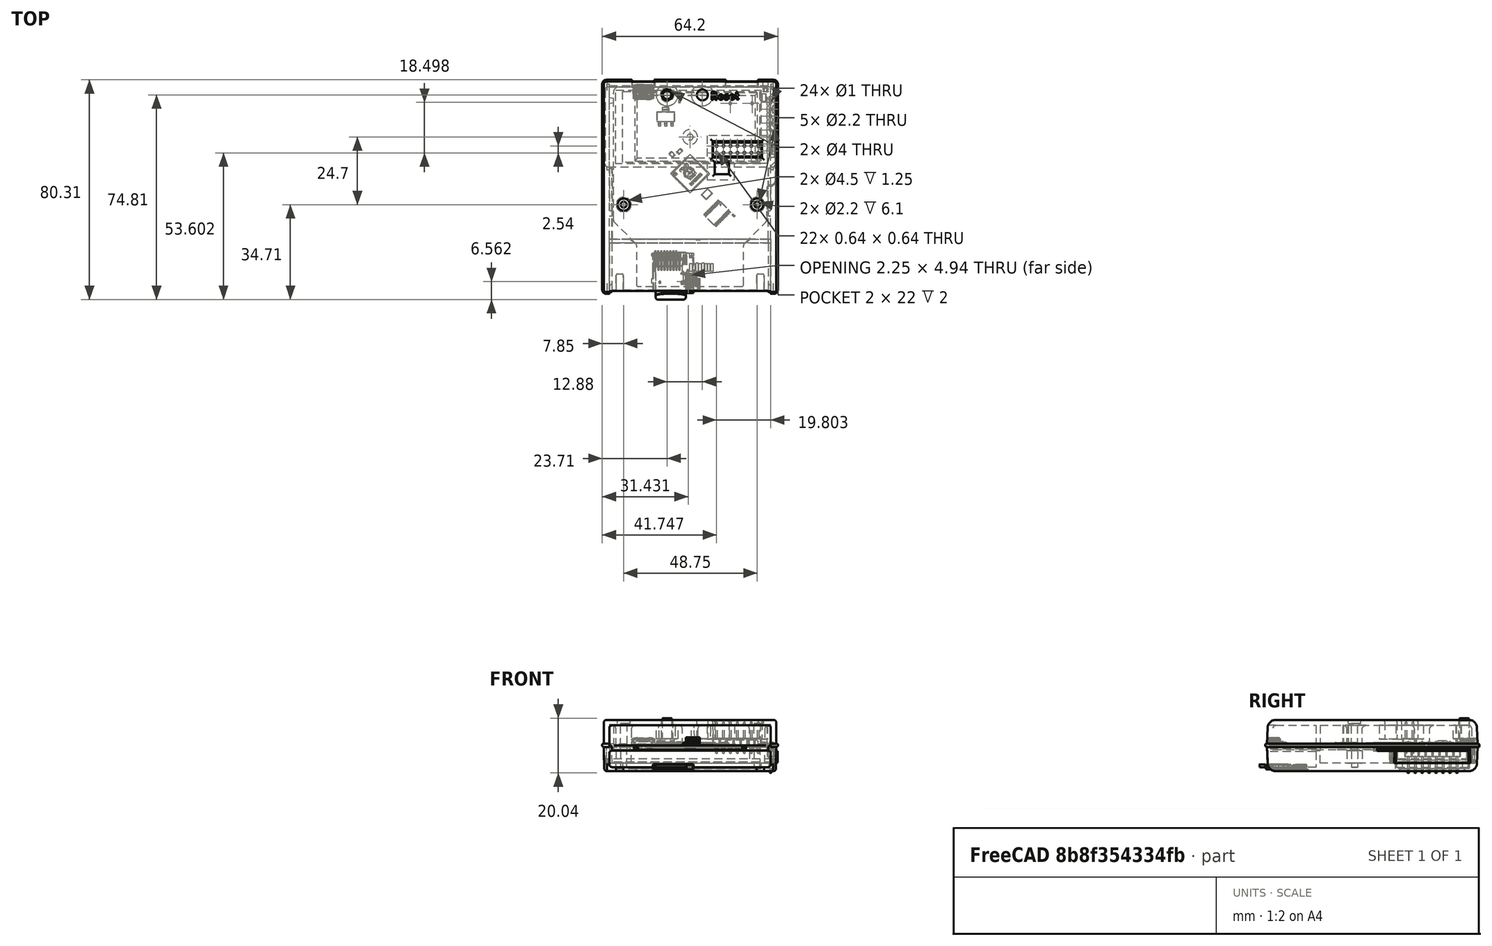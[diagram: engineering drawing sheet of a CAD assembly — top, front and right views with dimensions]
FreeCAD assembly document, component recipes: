
FREECAD ASSEMBLY — COMPONENT RECIPES ("DecentCart2350")

This assembly document has 7 components, labeled P0..P6 below (a component is one placed body or linked part). 7 of them carry a construction recipe — the FreeCAD feature program that regenerates the part from scratch, quoted from this document or its linked companion documents; the rest are supplied as boundary geometry only. No exploded tour is included for this assembly.
COMPONENT P0 — recipe-attached ("DecentCart", modeled in this document).
Construction recipe (the document's own serialized feature program — sketch geometry with constraints, then the solid features built on it; lengths are millimeters unless a unit is written):

FEATURE [PartDesign::SubShapeBinder] Binder009
  BindCopyOnChange = 0
  BindMode = 0
  ClaimChildren = false
  Context = -> Board_9dbe [Body004.Binder009.]
  Fuse = false
  MakeFace = true
  OffsetFill = false
  OffsetIntersection = false
  OffsetJoinType = 0
  OffsetOpenResult = false
  PartialLoad = false
  Relative = true
  Support = -> [Board_Geoms_9dbe[PCB_Sketch_9dbe.]]
  _Version = 2
FEATURE [Sketcher::SketchObject] Sketch028
  ArcFitTolerance = 1e-06
  AttachmentOffset = pos=(0,0,-4.95) rot=(0,0,1;0rad)
  AttachmentSupport = -> [XY_Plane]
  ExternalGeometry = -> [Binder009]
  FullyConstrained = true
  MakeInternals = false
  MapMode = 5
  Placement = pos=(0,0,-4.95) rot=(0,0,1;0rad)
  sketch-geometry (10):
    g0: LineSegment StartX=30.25 StartY=70 StartZ=0 EndX=-30.05 EndY=70 EndZ=0
    g1: LineSegment StartX=-31.05 StartY=69 StartZ=0 EndX=-31.05 EndY=41.8 EndZ=0
    g2: LineSegment StartX=-30.05 StartY=40.8 StartZ=0 EndX=30.25 EndY=40.8 EndZ=0
    g3: LineSegment StartX=31.25 StartY=41.8 StartZ=0 EndX=31.25 EndY=69 EndZ=0
    g4: ArcOfCircle CenterX=30.25 CenterY=69 CenterZ=0 NormalX=0 NormalY=0 NormalZ=1 AngleXU=0 Radius=1 StartAngle=1.6e-15 EndAngle=1.5708
    g5: ArcOfCircle CenterX=-30.05 CenterY=69 CenterZ=0 NormalX=0 NormalY=0 NormalZ=1 AngleXU=0 Radius=1 StartAngle=1.5708 EndAngle=3.14159
    g6: ArcOfCircle CenterX=-30.05 CenterY=41.8 CenterZ=0 NormalX=0 NormalY=0 NormalZ=1 AngleXU=0 Radius=1 StartAngle=3.14159 EndAngle=4.71239
    g7: ArcOfCircle CenterX=30.25 CenterY=41.8 CenterZ=0 NormalX=0 NormalY=0 NormalZ=1 AngleXU=0 Radius=1 StartAngle=4.71239 EndAngle=6.28319
    g8: GeomPoint [constr] X=31.25 Y=70 Z=0
    g9: GeomPoint [constr] X=-31.05 Y=40.8 Z=0
  constraints (24):
    c: Tangent(g0,g4) = -1.5708
    c: Tangent(g0,g5) = -1.5708
    c: Tangent(g1,g5) = -1.5708
    c: Tangent(g1,g6) = -1.5708
    c: Tangent(g2,g6) = -1.5708
    c: Tangent(g2,g7) = -1.5708
    c: Tangent(g3,g7) = -1.5708
    c: Tangent(g3,g4) = -1.5708
    c: Horizontal(g0)
    c: Horizontal(g2)
    c: Vertical(g1)
    c: Vertical(g3)
    c: Equal(g4,g5)
    c: Equal(g5,g6)
    c: Equal(g6,g7)
    c: PointOnObject(g8,g0)
    c: PointOnObject(g8,g3)
    c: PointOnObject(g9,g1)
    c: PointOnObject(g9,g2)
    c: Radius(g5) = 1
    c: PointOnObject(g3,g-3)
    c: PointOnObject(g0,g-4)
    c: DistanceX(g1,g3) = 62.3
    c: DistanceY(g2,g0) = 29.2
FEATURE [PartDesign::Pad] Pad018  label="Display PCB"
  Direction = (0,0,1)
  Length = 1.25
  Length2 = 10
  Profile = -> Sketch028
  ReferenceAxis = -> Sketch028 [N_Axis]
  Reversed = true
  Suppressed = false
  Type = 0
FEATURE [Sketcher::SketchObject] Sketch029
  ArcFitTolerance = 1e-06
  AttachmentSupport = -> [Pad018]
  ExternalGeometry = -> [Pad018]
  FullyConstrained = true
  MakeInternals = false
  MapMode = 5
  Placement = pos=(0,0,-6.2) rot=(1,0,0;3.14159rad)
  sketch-geometry (8):
    g0: LineSegment StartX=-24.65 StartY=-42.4 StartZ=0 EndX=-24.65 EndY=-68.4 EndZ=0
    g1: LineSegment StartX=-24.65 StartY=-68.4 StartZ=0 EndX=25.35 EndY=-68.4 EndZ=0
    g2: LineSegment StartX=25.35 StartY=-68.4 StartZ=0 EndX=25.35 EndY=-42.4 EndZ=0
    g3: LineSegment StartX=25.35 StartY=-42.4 StartZ=0 EndX=-24.65 EndY=-42.4 EndZ=0
    g4: GeomPoint [constr] X=0.1 Y=-55.4 Z=0
    g5: GeomPoint [constr] X=-31.05 Y=-55.4 Z=0
    g6: GeomPoint [constr] X=31.25 Y=-55.4 Z=0
    g7: LineSegment [constr] StartX=-31.05 StartY=-55.4 StartZ=0 EndX=31.25 EndY=-55.4 EndZ=0
  constraints (16):
    c: Coincident(g0,g1)
    c: Coincident(g1,g2)
    c: Coincident(g2,g3)
    c: Coincident(g3,g0)
    c: Vertical(g2)
    c: Horizontal(g1)
    c: Horizontal(g3)
    c: DistanceX(g3,g3) = 50
    c: DistanceY(g2,g2) = 26
    c: Symmetric(g-3,g-4,g4)
    c: Symmetric(g-3,g-3,g5)
    c: Symmetric(g-4,g-4,g6)
    c: Coincident(g7,g5)
    c: Coincident(g7,g6)
    c: Symmetric(g0,g0,g7)
    c: DistanceX(g-3,g0) = 6.4
FEATURE [PartDesign::Pad] Pad019  label="Display glass"
  BaseFeature = -> Pad018
  Direction = (0,0,-1)
  Length = 2
  Length2 = 10
  Profile = -> Sketch029
  ReferenceAxis = -> Sketch029 [N_Axis]
  Suppressed = false
  Type = 0
FEATURE [Sketcher::SketchObject] Sketch030  label="Display area"
  ArcFitTolerance = 1e-06
  AttachmentSupport = -> [Pad019]
  ExternalGeometry = -> [Pad019]
  FullyConstrained = true
  MakeInternals = false
  MapMode = 5
  Placement = pos=(0,0,-8.2) rot=(1,0,0;3.14159rad)
  sketch-geometry (7):
    g0: LineSegment StartX=-19.3 StartY=-43.9 StartZ=0 EndX=-19.3 EndY=-66.9 EndZ=0
    g1: LineSegment StartX=-19.3 StartY=-66.9 StartZ=0 EndX=23.7 EndY=-66.9 EndZ=0
    g2: LineSegment StartX=23.7 StartY=-66.9 StartZ=0 EndX=23.7 EndY=-43.9 EndZ=0
    g3: LineSegment StartX=23.7 StartY=-43.9 StartZ=0 EndX=-19.3 EndY=-43.9 EndZ=0
    g4: GeomPoint [constr] X=-31.05 Y=-55.4 Z=0
    g5: GeomPoint [constr] X=31.25 Y=-55.4 Z=0
    g6: LineSegment [constr] StartX=-31.05 StartY=-55.4 StartZ=0 EndX=31.25 EndY=-55.4 EndZ=0
  constraints (15):
    c: Coincident(g0,g1)
    c: Coincident(g1,g2)
    c: Coincident(g2,g3)
    c: Coincident(g3,g0)
    c: Vertical(g2)
    c: Horizontal(g1)
    c: Horizontal(g3)
    c: DistanceX(g3,g3) = 43
    c: DistanceY(g2,g2) = 23
    c: Symmetric(g-3,g-3,g4)
    c: Symmetric(g-4,g-4,g5)
    c: Coincident(g6,g4)
    c: Coincident(g6,g5)
    c: Symmetric(g0,g0,g6)
    c: DistanceX(g-3,g0) = 11.75
FEATURE [PartDesign::Body] Body004  label="Display"
  AllowCompound = false
  Group = -> [Binder009,Sketch028,Pad018,Sketch029,Pad019,Sketch030]
  Origin = -> Origin
  Tip = -> Pad019
COMPONENT P1 — recipe-attached ("BackBody", modeled in this document).
Construction recipe (the document's own serialized feature program — sketch geometry with constraints, then the solid features built on it; lengths are millimeters unless a unit is written):

FEATURE [Sketcher::SketchObject] Sketch
  ArcFitTolerance = 1e-06
  AttachmentSupport = -> [YZ_Plane008]
  FullyConstrained = true
  MakeInternals = false
  MapMode = 5
  Placement = pos=(0,0,0) rot=(0.57735,0.57735,0.57735;2.0944rad)
  sketch-geometry (7):
    g0: LineSegment StartX=-5 StartY=0 StartZ=0 EndX=-4.75 EndY=6.36769 EndZ=0
    g1: ArcOfCircle CenterX=-1.75231 CenterY=6.25 CenterZ=0 NormalX=0 NormalY=0 NormalZ=1 AngleXU=0 Radius=3 StartAngle=1.5708 EndAngle=3.10235
    g2: LineSegment StartX=-1.75231 StartY=9.25 StartZ=0 EndX=68.7523 EndY=9.25 EndZ=0
    g3: ArcOfCircle CenterX=68.7523 CenterY=6.25 CenterZ=0 NormalX=0 NormalY=0 NormalZ=1 AngleXU=0 Radius=3 StartAngle=0.0392405 EndAngle=1.5708
    g4: LineSegment StartX=71.75 StartY=6.36769 StartZ=0 EndX=72 EndY=0 EndZ=0
    g5: LineSegment StartX=72 StartY=0 StartZ=0 EndX=-5 EndY=0 EndZ=0
    g6: LineSegment [constr] StartX=33.5 StartY=0 StartZ=0 EndX=33.5 EndY=9.25 EndZ=0
  constraints (18):
    c: PointOnObject(g0,g-1)
    c: Tangent(g0,g1) = 1.5708
    c: Horizontal(g2)
    c: Tangent(g2,g3) = 1.5708
    c: Coincident(g4,g5)
    c: Coincident(g5,g0)
    c: Tangent(g3,g4) = 1.5708
    c: Tangent(g1,g2) = 1.5708
    c: Horizontal(g0,g3)
    c: Radius(g1) = 3
    c: DistanceX(g0,g3) = 76.5
    c: DistanceX(g0,g4) = 77
    c: PointOnObject(g6,g2)
    c: Symmetric(g1,g2,g6)
    c: DistanceY(g4,g2) = 9.25
    c: DistanceX(g0,g-3) = 5
    c: Symmetric(g0,g4,g6)
    c: PointOnObject(g6,g-1)
FEATURE [PartDesign::Pad] Pad  label="General shape of the thing"
  Direction = (1,0,0)
  Length = 63
  Length2 = 10
  Midplane = true
  Placement = pos=(0,0,0) rot=(1,1,1;2.0944rad)
  Profile = -> Sketch
  ReferenceAxis = -> Sketch [N_Axis]
  Suppressed = false
  Type = 0
FEATURE [PartDesign::Point] DatumPoint  label="Top middle"
  AttacherType = Attacher::AttachEnginePoint
  MapMode = 37
  Placement = pos=(0,70,-2) rot=(0,0,1;0rad)
FEATURE [PartDesign::Point] DatumPoint001  label="Bottom middle"
  AttacherType = Attacher::AttachEnginePoint
  MapMode = 37
  Placement = pos=(0,-1.42e-14,-2) rot=(0,0,1;0rad)
FEATURE [PartDesign::Line] DatumLine  label="Mid"
  AttacherType = Attacher::AttachEngineLine
  AttachmentSupport = -> [DatumPoint,DatumPoint001]
  Length = 20
  MapMode = 29
  Placement = pos=(0,70,-2) rot=(1,0,0;1.5708rad)
  ResizeMode = 0
FEATURE [PartDesign::Draft] Draft  label="Sides draft"
  Angle = 1
  Base = -> Pad [Face8,Face7]
  BaseFeature = -> Pad
  NeutralPlane = -> Pad [Face3]
  Placement = pos=(0,0,0) rot=(1,1,1;2.0944rad)
  SupportTransform = false
  Suppressed = false
FEATURE [PartDesign::Thickness] Thickness  label="Dig the insides"
  Base = -> Pad [Face6]
  BaseFeature = -> Pad
  Intersection = false
  Join = 0
  Mode = 0
  Reversed = true
  SupportTransform = false
  Suppressed = false
  Value = 2
FEATURE [Sketcher::SketchObject] Sketch001
  ArcFitTolerance = 1e-06
  AttachmentSupport = -> [Thickness]
  ExternalGeometry = -> [Thickness]
  FullyConstrained = true
  MakeInternals = false
  MapMode = 5
  Placement = pos=(0,0,-2e-16) rot=(1,0,0;3.14159rad)
  expr: Constraints[15] = .Constraints.offset
  expr: Constraints[16] = .Constraints.offset
  expr: Constraints[17] = .Constraints.offset
  sketch-geometry (16):
    g0: LineSegment StartX=-29.5 StartY=2.99846 StartZ=0 EndX=-29.5 EndY=-69.9985 EndZ=0
    g1: LineSegment StartX=-29.5 StartY=-69.9985 StartZ=0 EndX=29.5 EndY=-69.9985 EndZ=0
    g2: LineSegment StartX=29.5 StartY=-69.9985 StartZ=0 EndX=29.5 EndY=2.99846 EndZ=0
    g3: LineSegment StartX=29.5 StartY=2.99846 StartZ=0 EndX=-29.5 EndY=2.99846 EndZ=0
    g4: LineSegment StartX=-32.1 StartY=4.1 StartZ=0 EndX=-32.1 EndY=-71.1 EndZ=0
    g5: LineSegment StartX=-30.6 StartY=-72.6 StartZ=0 EndX=30.6 EndY=-72.6 EndZ=0
    g6: LineSegment StartX=32.1 StartY=-71.1 StartZ=0 EndX=32.1 EndY=4.1 EndZ=0
    g7: LineSegment StartX=30.6 StartY=5.6 StartZ=0 EndX=-30.6 EndY=5.6 EndZ=0
    g8: ArcOfCircle CenterX=-30.6 CenterY=4.1 CenterZ=0 NormalX=0 NormalY=0 NormalZ=1 AngleXU=0 Radius=1.5 StartAngle=1.5708 EndAngle=3.14159
    g9: GeomPoint [constr] X=-32.1 Y=5.6 Z=0
    g10: ArcOfCircle CenterX=30.6 CenterY=4.1 CenterZ=0 NormalX=0 NormalY=0 NormalZ=1 AngleXU=0 Radius=1.5 StartAngle=3e-16 EndAngle=1.5708
    g11: GeomPoint [constr] X=32.1 Y=5.6 Z=0
    g12: ArcOfCircle CenterX=30.6 CenterY=-71.1 CenterZ=0 NormalX=0 NormalY=0 NormalZ=1 AngleXU=0 Radius=1.5 StartAngle=4.71239 EndAngle=6.28319
    g13: GeomPoint [constr] X=32.1 Y=-72.6 Z=0
    g14: ArcOfCircle CenterX=-30.6 CenterY=-71.1 CenterZ=0 NormalX=0 NormalY=0 NormalZ=1 AngleXU=0 Radius=1.5 StartAngle=3.14159 EndAngle=4.71239
    g15: GeomPoint [constr] X=-32.1 Y=-72.6 Z=0
  constraints (38):
    c: Coincident(g0,g1)
    c: Coincident(g1,g2)
    c: Coincident(g2,g3)
    c: Coincident(g3,g0)
    c: Vertical(g0)
    c: Vertical(g2)
    c: Horizontal(g1)
    c: Horizontal(g3)
    c: Coincident(g0,g-8)
    c: Coincident(g1,g-10)
    c: Vertical(g4)
    c: Vertical(g6)
    c: Horizontal(g5)
    c: Horizontal(g7)
    c: DistanceX(g9,g-3) = 0.6  'offset'
    c: DistanceY(g-3,g9) = 0.6
    c: DistanceX(g-5,g13) = 0.6
    c: DistanceY(g13,g-5) = 0.6
    c: PointOnObject(g9,g4)
    c: PointOnObject(g9,g7)
    c: Tangent(g4,g8) = -1.5708
    c: Tangent(g7,g8) = -1.5708
    c: PointOnObject(g11,g7)
    c: PointOnObject(g11,g6)
    c: Tangent(g7,g10) = -1.5708
    c: Tangent(g6,g10) = -1.5708
    c: PointOnObject(g13,g6)
    c: PointOnObject(g13,g5)
    c: Tangent(g6,g12) = -1.5708
    c: Tangent(g5,g12) = -1.5708
    c: PointOnObject(g15,g5)
    c: PointOnObject(g15,g4)
    c: Tangent(g5,g14) = -1.5708
    c: Tangent(g4,g14) = -1.5708
    c: Radius(g8) = 1.5
    c: Equal(g8,g10)
    c: Equal(g8,g14)
    c: Equal(g8,g12)
FEATURE [PartDesign::Pad] Pad001  label="Rim"
  BaseFeature = -> Thickness
  Direction = (0,0,-1)
  Length = 1.27
  Length2 = 10
  Midplane = true
  Profile = -> Sketch001
  ReferenceAxis = -> Sketch001 [N_Axis]
  Refine = true
  Suppressed = false
  Type = 0
FEATURE [PartDesign::Plane] DatumPlane  label="Top of PCB"
  AttachmentOffset = pos=(0,0,-2) rot=(0,0,1;0rad)
  AttachmentSupport = -> [Pad001]
  Length = 80.0315
  MapMode = 2
  Placement = pos=(0,0,-2) rot=(0,0,1;0rad)
  ResizeMode = 0
  Width = 113.432
FEATURE [PartDesign::Plane] DatumPlane001  label="Bottom of PCB"
  AttachmentOffset = pos=(0,0,-0.4) rot=(0,0,1;0rad)
  AttachmentSupport = -> [XY_Plane008]
  Length = 80.0315
  MapMode = 5
  Placement = pos=(0,0,-0.4) rot=(0,0,1;0rad)
  ResizeMode = 0
  Width = 113.432
FEATURE [Sketcher::SketchObject] Sketch002
  ArcFitTolerance = 1e-06
  AttachmentOffset = pos=(0,0,-73) rot=(0,0,1;0rad)
  AttachmentSupport = -> [XZ_Plane008]
  FullyConstrained = true
  MakeInternals = false
  MapMode = 5
  Placement = pos=(0,73,-1.62e-14) rot=(1,0,0;1.5708rad)
  sketch-geometry (28):
    g0: LineSegment StartX=12.85 StartY=1.3 StartZ=0 EndX=12.85 EndY=-0.2 EndZ=0
    g1: LineSegment StartX=13.35 StartY=-0.7 StartZ=0 EndX=24.35 EndY=-0.7 EndZ=0
    g2: LineSegment StartX=24.85 StartY=-0.2 StartZ=0 EndX=24.85 EndY=1.3 EndZ=0
    g3: LineSegment StartX=24.35 StartY=1.8 StartZ=0 EndX=13.35 EndY=1.8 EndZ=0
    g4: LineSegment StartX=-21.35 StartY=1.95 StartZ=0 EndX=-21.35 EndY=-0.2 EndZ=0
    g5: LineSegment StartX=-20.85 StartY=-0.7 StartZ=0 EndX=-13.35 EndY=-0.7 EndZ=0
    g6: LineSegment StartX=-12.85 StartY=-0.2 StartZ=0 EndX=-12.85 EndY=1.95 EndZ=0
    g7: LineSegment StartX=-13.35 StartY=2.45 StartZ=0 EndX=-20.85 EndY=2.45 EndZ=0
    g8: ArcOfCircle CenterX=13.35 CenterY=1.3 CenterZ=0 NormalX=0 NormalY=0 NormalZ=1 AngleXU=0 Radius=0.5 StartAngle=1.5708 EndAngle=3.14159
    g9: GeomPoint [constr] X=12.85 Y=1.8 Z=0
    g10: ArcOfCircle CenterX=13.35 CenterY=-0.2 CenterZ=0 NormalX=0 NormalY=0 NormalZ=1 AngleXU=0 Radius=0.5 StartAngle=3.14159 EndAngle=4.71239
    g11: GeomPoint [constr] X=12.85 Y=-0.7 Z=0
    g12: ArcOfCircle CenterX=24.35 CenterY=1.3 CenterZ=0 NormalX=0 NormalY=0 NormalZ=1 AngleXU=0 Radius=0.5 StartAngle=2e-16 EndAngle=1.5708
    g13: GeomPoint [constr] X=24.85 Y=1.8 Z=0
    g14: ArcOfCircle CenterX=24.35 CenterY=-0.2 CenterZ=0 NormalX=0 NormalY=0 NormalZ=1 AngleXU=0 Radius=0.5 StartAngle=4.71239 EndAngle=6.28319
    g15: GeomPoint [constr] X=24.85 Y=-0.7 Z=0
    g16: ArcOfCircle CenterX=-20.85 CenterY=1.95 CenterZ=0 NormalX=0 NormalY=0 NormalZ=1 AngleXU=0 Radius=0.5 StartAngle=1.5708 EndAngle=3.14159
    g17: GeomPoint [constr] X=-21.35 Y=2.45 Z=0
    g18: ArcOfCircle CenterX=-20.85 CenterY=-0.2 CenterZ=0 NormalX=0 NormalY=0 NormalZ=1 AngleXU=0 Radius=0.5 StartAngle=3.14159 EndAngle=4.71239
    g19: GeomPoint [constr] X=-21.35 Y=-0.7 Z=0
    g20: ArcOfCircle CenterX=-13.35 CenterY=-0.2 CenterZ=0 NormalX=0 NormalY=0 NormalZ=1 AngleXU=0 Radius=0.5 StartAngle=4.71239 EndAngle=6.28319
    g21: GeomPoint [constr] X=-12.85 Y=-0.7 Z=0
    g22: ArcOfCircle CenterX=-13.35 CenterY=1.95 CenterZ=0 NormalX=0 NormalY=0 NormalZ=1 AngleXU=0 Radius=0.5 StartAngle=0 EndAngle=1.5708
    g23: GeomPoint [constr] X=-12.85 Y=2.45 Z=0
    g24: ArcOfCircle CenterX=28.1 CenterY=0.4 CenterZ=0 NormalX=0 NormalY=0 NormalZ=1 AngleXU=0 Radius=0.5 StartAngle=4.71239 EndAngle=7.85398
    g25: ArcOfCircle CenterX=27.1 CenterY=0.4 CenterZ=0 NormalX=0 NormalY=0 NormalZ=1 AngleXU=0 Radius=0.5 StartAngle=1.5708 EndAngle=4.71239
    g26: LineSegment StartX=28.1 StartY=-0.1 StartZ=0 EndX=27.1 EndY=-0.1 EndZ=0
    g27: LineSegment StartX=28.1 StartY=0.9 StartZ=0 EndX=27.1 EndY=0.9 EndZ=0
  constraints (66):
    c: Vertical(g0)
    c: Vertical(g2)
    c: Horizontal(g1)
    c: Horizontal(g3)
    c: Vertical(g4)
    c: Vertical(g6)
    c: Horizontal(g5)
    c: Horizontal(g7)
    c: PointOnObject(g9,g3)
    c: PointOnObject(g9,g0)
    c: Tangent(g3,g8) = -1.5708
    c: Tangent(g0,g8) = -1.5708
    c: Radius(g8) = 0.5  'fillet'
    c: PointOnObject(g11,g1)
    c: PointOnObject(g11,g0)
    c: Tangent(g1,g10) = -1.5708
    c: Tangent(g0,g10) = -1.5708
    c: PointOnObject(g13,g2)
    c: PointOnObject(g13,g3)
    c: Tangent(g2,g12) = -1.5708
    c: Tangent(g3,g12) = -1.5708
    c: PointOnObject(g15,g2)
    c: PointOnObject(g15,g1)
    c: Tangent(g2,g14) = -1.5708
    c: Tangent(g1,g14) = -1.5708
    c: Equal(g8,g12)
    c: Equal(g8,g14)
    c: Equal(g8,g10)
    c: DistanceX(g-1,g0) = 12.85
    c: DistanceX(g0,g2) = 12
    c: PointOnObject(g17,g7)
    c: PointOnObject(g17,g4)
    c: Tangent(g7,g16) = -1.5708
    c: Tangent(g4,g16) = -1.5708
    c: PointOnObject(g19,g4)
    c: PointOnObject(g19,g5)
    c: Tangent(g4,g18) = -1.5708
    c: Tangent(g5,g18) = -1.5708
    c: PointOnObject(g21,g5)
    c: PointOnObject(g21,g6)
    c: Tangent(g5,g20) = -1.5708
    c: Tangent(g6,g20) = -1.5708
    c: PointOnObject(g23,g6)
    c: PointOnObject(g23,g7)
    c: Tangent(g6,g22) = -1.5708
    c: Tangent(g7,g22) = -1.5708
    c: Equal(g22,g8)
    c: Equal(g16,g22)
    c: Equal(g16,g20)
    c: Equal(g16,g18)
    c: DistanceX(g6,g-1) = 12.85
    c: DistanceX(g4,g6) = 8.5
    c: DistanceY(g5,g7) = 3.15
    c: DistanceY(g-1,g7) = 2.45
    c: DistanceY(g3,g7) = 0.65
    c: Horizontal(g1,g5)
    c: Tangent(g24,g26) = 1.5708
    c: Tangent(g24,g27) = -1.5708
    c: Tangent(g25,g26) = 1.5708
    c: Tangent(g25,g27) = -1.5708
    c: Equal(g24,g25)
    c: Horizontal(g26)
    c: DistanceY(g24,g24) = 1
    c: DistanceX(g25,g24) = 1
    c: DistanceY(g-1,g24) = 0.4
    c: DistanceX(g-1,g25) = 27.1
FEATURE [PartDesign::Pocket] Pocket  label="SD and USB slots"
  BaseFeature = -> Pad001
  Direction = (0,1,-2e-16)
  Length = 4
  Length2 = 5
  Profile = -> Sketch002
  ReferenceAxis = -> Sketch002 [N_Axis]
  Reversed = true
  Suppressed = false
  Type = 0
FEATURE [Sketcher::SketchObject] Sketch003
  ArcFitTolerance = 1e-06
  AttachmentOffset = pos=(0,0,-2) rot=(0,0,1;0rad)
  AttachmentSupport = -> [Pocket]
  FullyConstrained = true
  MakeInternals = false
  MapMode = 5
  Placement = pos=(0,2e-15,7.25) rot=(0,0,1;0rad)
  sketch-geometry (4):
    g0: Circle CenterX=-8.39 CenterY=67.1 CenterZ=0 NormalX=0 NormalY=0 NormalZ=1 AngleXU=0 Radius=4
    g1: Circle CenterX=4.49 CenterY=67.1 CenterZ=0 NormalX=0 NormalY=0 NormalZ=1 AngleXU=0 Radius=4
    g2: Circle CenterX=-8.39 CenterY=67.1 CenterZ=0 NormalX=0 NormalY=0 NormalZ=1 AngleXU=0 Radius=2
    g3: Circle CenterX=4.49 CenterY=67.1 CenterZ=0 NormalX=0 NormalY=0 NormalZ=1 AngleXU=0 Radius=2
  constraints (10):
    c: Horizontal(g0,g1)
    c: Equal(g0,g1)
    c: Diameter(g0) = 8
    c: Distance(g1,g-2) = 4.49
    c: Distance(g0,g-2) = 8.39
    c: Distance(g1,g-1) = 67.1
    c: Diameter(g2) = 4
    c: Coincident(g2,g0)
    c: Coincident(g3,g1)
    c: Equal(g3,g2)
FEATURE [PartDesign::Pad] Pad002  label="Button columns"
  BaseFeature = -> Pocket
  Direction = (0,0,1)
  Length = 4.85
  Length2 = 10
  Profile = -> Sketch003 [Edge2,Edge1]
  ReferenceAxis = -> Sketch003 [N_Axis]
  Reversed = true
  Suppressed = false
  Type = 0
FEATURE [PartDesign::Pocket] Pocket001  label="Button pockets"
  BaseFeature = -> Pad002
  Direction = (0,0,-1)
  Length = 5
  Length2 = 5
  Midplane = true
  Profile = -> Sketch003 [Edge4,Edge3]
  ReferenceAxis = -> Sketch003 [N_Axis]
  Suppressed = false
  Type = 1
FEATURE [Sketcher::SketchObject] Sketch005
  ArcFitTolerance = 1e-06
  AttachmentSupport = -> [XZ_Plane008]
  ExternalGeometry = -> [Pocket001]
  FullyConstrained = true
  MakeInternals = false
  MapMode = 5
  Placement = pos=(0,0,0) rot=(1,0,0;1.5708rad)
  sketch-geometry (8):
    g0: LineSegment StartX=-29.5 StartY=-0.635 StartZ=0 EndX=29.5 EndY=-0.635 EndZ=0
    g1: LineSegment StartX=29.5 StartY=-0.635 StartZ=0 EndX=29.5 EndY=6.25 EndZ=0
    g2: LineSegment StartX=28.5 StartY=7.25 StartZ=0 EndX=-28.5 EndY=7.25 EndZ=0
    g3: LineSegment StartX=-29.5 StartY=6.25 StartZ=0 EndX=-29.5 EndY=-0.635 EndZ=0
    g4: ArcOfCircle CenterX=-28.5 CenterY=6.25 CenterZ=0 NormalX=0 NormalY=0 NormalZ=1 AngleXU=0 Radius=1 StartAngle=1.5708 EndAngle=3.14159
    g5: GeomPoint [constr] X=-29.5 Y=7.25 Z=0
    g6: ArcOfCircle CenterX=28.5 CenterY=6.25 CenterZ=0 NormalX=0 NormalY=0 NormalZ=1 AngleXU=0 Radius=1 StartAngle=4e-16 EndAngle=1.5708
    g7: GeomPoint [constr] X=29.5 Y=7.25 Z=0
  constraints (18):
    c: Coincident(g0,g1)
    c: Coincident(g3,g0)
    c: Horizontal(g0)
    c: Horizontal(g2)
    c: Vertical(g1)
    c: Vertical(g3)
    c: Coincident(g0,g-4)
    c: Coincident(g7,g-3)
    c: PointOnObject(g5,g3)
    c: PointOnObject(g5,g2)
    c: Tangent(g3,g4) = -1.5708
    c: Tangent(g2,g4) = -1.5708
    c: PointOnObject(g7,g2)
    c: PointOnObject(g7,g1)
    c: Tangent(g2,g6) = -1.5708
    c: Tangent(g1,g6) = -1.5708
    c: Equal(g4,g6)
    c: Radius(g4) = 1
FEATURE [PartDesign::Pocket] Pocket002  label="PCB opening"
  BaseFeature = -> Pocket001
  Direction = (0,1,-2e-16)
  Length = 5
  Length2 = 5
  Profile = -> Sketch005
  ReferenceAxis = -> Sketch005 [N_Axis]
  Refine = true
  Reversed = true
  Suppressed = false
  Type = 1
FEATURE [Sketcher::SketchObject] Sketch006
  ArcFitTolerance = 1e-06
  AttachmentSupport = -> [Pocket002]
  FullyConstrained = true
  MakeInternals = false
  MapMode = 5
  Placement = pos=(0,2e-15,9.25) rot=(0,0,1;0rad)
  sketch-geometry (9):
    g0: Circle CenterX=-24.25 CenterY=27 CenterZ=0 NormalX=0 NormalY=0 NormalZ=1 AngleXU=0 Radius=2.75
    g1: Circle CenterX=24.5 CenterY=27 CenterZ=0 NormalX=0 NormalY=0 NormalZ=1 AngleXU=0 Radius=2.75
    g2: Circle CenterX=0 CenterY=51.7 CenterZ=0 NormalX=0 NormalY=0 NormalZ=1 AngleXU=0 Radius=2.75
    g3: Circle CenterX=0 CenterY=51.7 CenterZ=0 NormalX=0 NormalY=0 NormalZ=1 AngleXU=0 Radius=1.1
    g4: Circle CenterX=-24.25 CenterY=27 CenterZ=0 NormalX=0 NormalY=0 NormalZ=1 AngleXU=0 Radius=1.1
    g5: Circle CenterX=24.5 CenterY=27 CenterZ=0 NormalX=0 NormalY=0 NormalZ=1 AngleXU=0 Radius=1.1
    g6: Circle CenterX=0 CenterY=51.7 CenterZ=0 NormalX=0 NormalY=0 NormalZ=1 AngleXU=0 Radius=2.25
    g7: Circle CenterX=24.5 CenterY=27 CenterZ=0 NormalX=0 NormalY=0 NormalZ=1 AngleXU=0 Radius=2.25
    g8: Circle CenterX=-24.25 CenterY=27 CenterZ=0 NormalX=0 NormalY=0 NormalZ=1 AngleXU=0 Radius=2.25
  constraints (21):
    c: PointOnObject(g2,g-2)
    c: Coincident(g3,g2)
    c: Coincident(g4,g0)
    c: Coincident(g5,g1)
    c: Equal(g3,g4)
    c: Equal(g3,g5)
    c: Equal(g2,g1)
    c: Equal(g2,g0)
    c: Diameter(g3) = 2.2
    c: Diameter(g2) = 5.5
    c: DistanceY(g-1,g2) = 51.7
    c: DistanceX(g-1,g1) = 24.5
    c: DistanceY(g-1,g1) = 27
    c: Diameter(g6) = 4.5
    c: Coincident(g6,g2)
    c: Coincident(g7,g1)
    c: Coincident(g8,g0)
    c: Equal(g6,g8)
    c: Equal(g6,g7)
    c: DistanceX(g0,g-1) = 24.25
    c: Horizontal(g0,g1)
FEATURE [PartDesign::Pad] Pad005  label="Screw columns"
  BaseFeature = -> Pocket002
  Direction = (0,0,1)
  Length = 10
  Length2 = 10
  Profile = -> Sketch006 [Edge3,Edge1,Edge2]
  ReferenceAxis = -> Sketch006 [N_Axis]
  Refine = true
  Reversed = true
  Suppressed = false
  Type = 3
  UpToFace = -> DatumPlane001
FEATURE [PartDesign::Pocket] Pocket003  label="Screw head recess"
  BaseFeature = -> Pad005
  Direction = (0,0,-1)
  Length = 1.25
  Length2 = 5
  Profile = -> Sketch006 [Edge9,Edge8]
  ReferenceAxis = -> Sketch006 [N_Axis]
  Suppressed = false
  Type = 0
FEATURE [PartDesign::Pocket] Pocket004  label="Screw tunnels"
  BaseFeature = -> Pocket003
  Direction = (0,0,-1)
  Length = 5
  Length2 = 5
  Profile = -> Sketch006 [Edge5,Edge6]
  ReferenceAxis = -> Sketch006 [N_Axis]
  Suppressed = false
  Type = 1
FEATURE [Sketcher::SketchObject] Sketch007
  ArcFitTolerance = 1e-06
  AttachmentSupport = -> [Pocket004]
  ExternalGeometry = -> [Pocket004]
  FullyConstrained = true
  MakeInternals = false
  MapMode = 5
  Placement = pos=(0,2.6e-15,7.25) rot=(1,0,0;3.14159rad)
  sketch-geometry (12):
    g0: LineSegment StartX=-29.5 StartY=-22.75 StartZ=0 EndX=-28 EndY=-23 EndZ=0
    g1: LineSegment StartX=-28 StartY=-23 StartZ=0 EndX=-28 EndY=-24.5 EndZ=0
    g2: LineSegment StartX=-28 StartY=-24.5 StartZ=0 EndX=-29.5 EndY=-24.75 EndZ=0
    g3: LineSegment StartX=-29.5 StartY=-24.75 StartZ=0 EndX=-29.5 EndY=-22.75 EndZ=0
    g4: LineSegment StartX=-29.5 StartY=-64 StartZ=0 EndX=-28 EndY=-64.25 EndZ=0
    g5: LineSegment StartX=-28 StartY=-64.25 StartZ=0 EndX=-28 EndY=-65.75 EndZ=0
    g6: LineSegment StartX=-28 StartY=-65.75 StartZ=0 EndX=-29.5 EndY=-66 EndZ=0
    g7: LineSegment StartX=-29.5 StartY=-66 StartZ=0 EndX=-29.5 EndY=-64 EndZ=0
    g8: LineSegment StartX=29.5 StartY=-22.75 StartZ=0 EndX=28 EndY=-23 EndZ=0
    g9: LineSegment StartX=28 StartY=-23 StartZ=0 EndX=28 EndY=-24.5 EndZ=0
    g10: LineSegment StartX=28 StartY=-24.5 StartZ=0 EndX=29.5 EndY=-24.75 EndZ=0
    g11: LineSegment StartX=29.5 StartY=-24.75 StartZ=0 EndX=29.5 EndY=-22.75 EndZ=0
  constraints (36):
    c: Coincident(g0,g1)
    c: Coincident(g1,g2)
    c: Coincident(g2,g3)
    c: Coincident(g3,g0)
    c: DistanceY(g1,g1) = 1.5
    c: DistanceY(g3,g3) = 2
    c: Equal(g0,g2)
    c: DistanceY(g0,g-1) = 23
    c: Coincident(g4,g5)
    c: Coincident(g5,g6)
    c: Coincident(g6,g7)
    c: Coincident(g7,g4)
    c: DistanceY(g5,g5) = 1.5
    c: DistanceY(g7,g7) = 2
    c: Equal(g4,g6)
    c: Coincident(g8,g9)
    c: Coincident(g9,g10)
    c: Coincident(g10,g11)
    c: Coincident(g11,g8)
    c: DistanceY(g9,g9) = 1.5
    c: DistanceY(g11,g11) = 2
    c: Equal(g8,g10)
    c: PointOnObject(g0,g-3)
    c: PointOnObject(g2,g-3)
    c: PointOnObject(g1,g-4)
    c: PointOnObject(g0,g-4)
    c: PointOnObject(g4,g-3)
    c: PointOnObject(g6,g-3)
    c: PointOnObject(g4,g-4)
    c: PointOnObject(g5,g-4)
    c: DistanceY(g4,g-1) = 64
    c: PointOnObject(g8,g-5)
    c: PointOnObject(g10,g-5)
    c: PointOnObject(g8,g-6)
    c: PointOnObject(g9,g-6)
    c: Horizontal(g8,g0)
FEATURE [PartDesign::Pad] Pad006  label="Side padding"
  BaseFeature = -> Pocket004
  Direction = (0,0,-1)
  Length = 10
  Length2 = 10
  Profile = -> Sketch007
  ReferenceAxis = -> Sketch007 [N_Axis]
  Refine = true
  Suppressed = false
  Type = 3
  UpToFace = -> Pocket004 [Face52]
FEATURE [PartDesign::Fillet] Fillet  label="Wide fillet"
  Base = -> Pad006 [Edge49,Edge122]
  BaseFeature = -> Pad006
  Radius = 1
  SupportTransform = false
  Suppressed = false
  UseAllEdges = false
FEATURE [PartDesign::Fillet] Fillet001  label="Thin fillet"
  Base = -> Fillet [Edge205,Edge78,Edge238,Edge168,Edge265,Edge252]
  BaseFeature = -> Fillet
  Radius = 0.5
  SupportTransform = false
  Suppressed = false
  UseAllEdges = false
FEATURE [PartDesign::Fillet] Fillet002  label="Column base fillet"
  Base = -> Fillet001 [Edge217,Edge218,Edge219]
  BaseFeature = -> Fillet001
  Radius = 1.5
  SupportTransform = false
  Suppressed = false
  UseAllEdges = false
FEATURE [Sketcher::SketchObject] Sketch008
  ArcFitTolerance = 1e-06
  AttachmentSupport = -> [Fillet002]
  ExternalGeometry = -> [Fillet002]
  FullyConstrained = true
  MakeInternals = false
  MapMode = 5
  Placement = pos=(0,2.6e-15,7.25) rot=(1,0,0;3.14159rad)
  sketch-geometry (4):
    g0: LineSegment StartX=-29.5 StartY=-12.9193 StartZ=0 EndX=-29.5 EndY=-14.4193 EndZ=0
    g1: LineSegment StartX=-29.5 StartY=-14.4193 StartZ=0 EndX=29.5 EndY=-14.4193 EndZ=0
    g2: LineSegment StartX=29.5 StartY=-14.4193 StartZ=0 EndX=29.5 EndY=-12.9193 EndZ=0
    g3: LineSegment StartX=29.5 StartY=-12.9193 StartZ=0 EndX=-29.5 EndY=-12.9193 EndZ=0
  constraints (12):
    c: Coincident(g0,g1)
    c: Coincident(g1,g2)
    c: Coincident(g2,g3)
    c: Coincident(g3,g0)
    c: Vertical(g0)
    c: Vertical(g2)
    c: Horizontal(g1)
    c: Horizontal(g3)
    c: PointOnObject(g2,g-3)
    c: PointOnObject(g0,g-4)
    c: DistanceY(g0,g0) = 1.5
    c: DistanceY(g0,g-5) = 17.5
FEATURE [PartDesign::Pad] Pad007  label="Lower barrier"
  BaseFeature = -> Fillet002
  Direction = (0,0,-1)
  Length = 6.6
  Length2 = 10
  Profile = -> Sketch008
  ReferenceAxis = -> Sketch008 [N_Axis]
  Refine = true
  Suppressed = false
  Type = 3
  UpToFace = -> DatumPlane001 [Plane]
FEATURE [Sketcher::SketchObject] Sketch009
  ArcFitTolerance = 1e-06
  AttachmentSupport = -> [Pad007]
  ExternalGeometry = -> [Pad007]
  FullyConstrained = true
  MakeInternals = false
  MapMode = 5
  Placement = pos=(0,0,-0.4) rot=(1,0,0;3.14159rad)
  sketch-geometry (8):
    g0: LineSegment StartX=-29.5 StartY=-12.9193 StartZ=0 EndX=-29.5 EndY=-14.4193 EndZ=0
    g1: LineSegment StartX=-29.5 StartY=-14.4193 StartZ=0 EndX=-22 EndY=-14.4193 EndZ=0
    g2: LineSegment StartX=-22 StartY=-14.4193 StartZ=0 EndX=-20.5 EndY=-12.9193 EndZ=0
    g3: LineSegment StartX=-20.5 StartY=-12.9193 StartZ=0 EndX=-29.5 EndY=-12.9193 EndZ=0
    g4: LineSegment StartX=29.5 StartY=-12.9193 StartZ=0 EndX=20.5 EndY=-12.9193 EndZ=0
    g5: LineSegment StartX=20.5 StartY=-12.9193 StartZ=0 EndX=22 EndY=-14.4193 EndZ=0
    g6: LineSegment StartX=22 StartY=-14.4193 StartZ=0 EndX=29.5 EndY=-14.4193 EndZ=0
    g7: LineSegment StartX=29.5 StartY=-14.4193 StartZ=0 EndX=29.5 EndY=-12.9193 EndZ=0
  constraints (20):
    c: Coincident(g0,g1)
    c: Coincident(g1,g2)
    c: Coincident(g2,g3)
    c: Coincident(g3,g0)
    c: Vertical(g0)
    c: Horizontal(g1)
    c: Horizontal(g3)
    c: Coincident(g4,g5)
    c: Coincident(g6,g7)
    c: Coincident(g7,g4)
    c: Horizontal(g6)
    c: Symmetric(g2,g4,g-2)
    c: DistanceX(g2,g4) = 41
    c: Coincident(g6,g5)
    c: Angle(g5,g4) = 0.785398
    c: Angle(g3,g2) = 0.785398
    c: Horizontal(g4)
    c: Coincident(g4,g-3)
    c: Coincident(g6,g-4)
    c: Coincident(g0,g-4)
FEATURE [PartDesign::Pad] Pad008  label="Top barrier"
  BaseFeature = -> Pad007
  Direction = (0,0,-1)
  Length = 1.6
  Length2 = 10
  Profile = -> Sketch009
  ReferenceAxis = -> Sketch009 [N_Axis]
  Refine = true
  Suppressed = false
  Type = 0
FEATURE [Part::Part2DObjectPython] ShapeString  label="Reset"  # Draft 2D object (typed FeaturePython)
  FontFile = <path>
  Fuse = false
  Justification = 6
  JustificationReference = 0
  KeepLeftMargin = false
  MakeFace = true
  ObliqueAngle = 0
  Placement = pos=(7.8198,65.3531,9.25) rot=(0,0,-0.999058;0rad)
  ScaleToSize = true
  Size = 3
  String = Reset
  Tracking = 0
FEATURE [PartDesign::Pocket] Pocket011  label="Reset legend"
  BaseFeature = -> Pad008
  Direction = (0,0,-1)
  Length = 0.3
  Length2 = 5
  Profile = -> ShapeString
  ReferenceAxis = -> ShapeString [N_Axis]
  Suppressed = false
  Type = 0
FEATURE [Sketcher::SketchObject] Sketch024
  ArcFitTolerance = 1e-06
  AttachmentSupport = -> [Pocket011]
  FullyConstrained = true
  MakeInternals = false
  MapMode = 5
  Placement = pos=(0,14.4193,0) rot=(0,0.707107,0.707107;3.14159rad)
  sketch-geometry (4):
    g0: LineSegment StartX=-2.1 StartY=0 StartZ=0 EndX=-2.1 EndY=0.2 EndZ=0
    g1: LineSegment StartX=-2.1 StartY=0.2 StartZ=0 EndX=-3.85 EndY=0.2 EndZ=0
    g2: LineSegment StartX=-3.85 StartY=0.2 StartZ=0 EndX=-3.85 EndY=0 EndZ=0
    g3: LineSegment StartX=-3.85 StartY=0 StartZ=0 EndX=-2.1 EndY=0 EndZ=0
  constraints (12):
    c: Coincident(g0,g1)
    c: Coincident(g1,g2)
    c: Coincident(g2,g3)
    c: Coincident(g3,g0)
    c: Vertical(g0)
    c: Vertical(g2)
    c: Horizontal(g1)
    c: Horizontal(g3)
    c: PointOnObject(g0,g-1)
    c: DistanceX(g1,g1) = 1.75
    c: DistanceY(g2,g2) = 0.2
    c: DistanceX(g0,g-1) = 2.1
FEATURE [PartDesign::Pocket] Pocket017  label="SmallCapPocket"
  BaseFeature = -> Pocket011
  Direction = (0,-1,2e-16)
  Length = 0.3
  Length2 = 5
  Profile = -> Sketch024
  ReferenceAxis = -> Sketch024 [N_Axis]
  Suppressed = false
  Type = 0
FEATURE [Sketcher::SketchObject] Sketch025
  ArcFitTolerance = 1e-06
  AttachmentSupport = -> [Pocket017]
  ExternalGeometry = -> [Pocket017]
  FullyConstrained = true
  MakeInternals = false
  MapMode = 5
  Placement = pos=(5e-16,0,-0.635) rot=(1,0,0;3.14159rad)
  sketch-geometry (4):
    g0: ArcOfCircle CenterX=29.5 CenterY=-36 CenterZ=0 NormalX=0 NormalY=0 NormalZ=1 AngleXU=0 Radius=2.1 StartAngle=-1.8e-15 EndAngle=3.14159
    g1: ArcOfCircle CenterX=29.5 CenterY=-68.2 CenterZ=0 NormalX=0 NormalY=0 NormalZ=1 AngleXU=0 Radius=2.1 StartAngle=3.14159 EndAngle=6.28319
    g2: LineSegment StartX=31.6 StartY=-36 StartZ=0 EndX=31.6 EndY=-68.2 EndZ=0
    g3: LineSegment StartX=27.4 StartY=-36 StartZ=0 EndX=27.4 EndY=-68.2 EndZ=0
  constraints (10):
    c: Tangent(g0,g2) = 1.5708
    c: Tangent(g0,g3) = -1.5708
    c: Tangent(g1,g2) = 1.5708
    c: Tangent(g1,g3) = -1.5708
    c: Equal(g0,g1)
    c: Vertical(g3)
    c: PointOnObject(g0,g-3)
    c: PointOnObject(g0,g-4)
    c: DistanceY(g2,g2) = 32.2
    c: DistanceY(g0,g-1) = 36
FEATURE [PartDesign::Pocket] Pocket018  label="SidePCBPocket"
  BaseFeature = -> Pocket017
  Direction = (0,0,1)
  Length = 0.2
  Length2 = 5
  Profile = -> Sketch025
  ReferenceAxis = -> Sketch025 [N_Axis]
  Suppressed = false
  Type = 0
FEATURE [Sketcher::SketchObject] Sketch026
  ArcFitTolerance = 1e-06
  AttachmentSupport = -> [Pocket018]
  ExternalGeometry = -> [Pocket018]
  FullyConstrained = true
  MakeInternals = false
  MapMode = 5
  Placement = pos=(0,0,-0.435) rot=(1,0,0;3.14159rad)
  sketch-geometry (5):
    g0: ArcOfCircle CenterX=29.5 CenterY=-46.5 CenterZ=0 NormalX=0 NormalY=0 NormalZ=1 AngleXU=0 Radius=0.75 StartAngle=1.3e-15 EndAngle=3.14159
    g1: ArcOfCircle CenterX=29.5 CenterY=-64.5 CenterZ=0 NormalX=0 NormalY=0 NormalZ=1 AngleXU=0 Radius=0.75 StartAngle=3.14159 EndAngle=6.28319
    g2: LineSegment StartX=30.25 StartY=-46.5 StartZ=0 EndX=30.25 EndY=-64.5 EndZ=0
    g3: LineSegment StartX=28.75 StartY=-46.5 StartZ=0 EndX=28.75 EndY=-64.5 EndZ=0
    g4: Circle CenterX=29.5 CenterY=-68.25 CenterZ=0 NormalX=0 NormalY=0 NormalZ=1 AngleXU=0 Radius=1
  constraints (13):
    c: Tangent(g0,g2) = 1.5708
    c: Tangent(g0,g3) = -1.5708
    c: Tangent(g1,g2) = 1.5708
    c: Tangent(g1,g3) = -1.5708
    c: Equal(g0,g1)
    c: Vertical(g2)
    c: DistanceX(g0,g0) = 0.75
    c: DistanceY(g1,g0) = 18
    c: DistanceY(g0,g-1) = 46.5
    c: PointOnObject(g0,g-3)
    c: Diameter(g4) = 2
    c: DistanceY(g4,g1) = 3.75
    c: Vertical(g4,g0)
FEATURE [PartDesign::Pocket] Pocket019  label="SideComponentPocket"
  BaseFeature = -> Pocket018
  Direction = (0,0,1)
  Length = 1.5
  Length2 = 5
  Profile = -> Sketch026
  ReferenceAxis = -> Sketch026 [N_Axis]
  Suppressed = false
  Type = 0
FEATURE [Sketcher::SketchObject] Sketch027
  ArcFitTolerance = 1e-06
  AttachmentSupport = -> [Pocket019]
  FullyConstrained = true
  MakeInternals = false
  MapMode = 5
  Placement = pos=(0,0,9.25) rot=(0,0,1;0rad)
  sketch-geometry (18):
    g0: LineSegment StartX=8.27 StartY=50.16 StartZ=0 EndX=8.27 EndY=44.16 EndZ=0
    g1: LineSegment StartX=8.27 StartY=44.16 StartZ=0 EndX=26.27 EndY=44.16 EndZ=0
    g2: LineSegment StartX=26.27 StartY=44.16 StartZ=0 EndX=26.27 EndY=50.16 EndZ=0
    g3: LineSegment StartX=26.27 StartY=50.16 StartZ=0 EndX=8.27 EndY=50.16 EndZ=0
    g4: LineSegment StartX=9.005 StartY=42.49 StartZ=0 EndX=9.005 EndY=38.09 EndZ=0
    g5: LineSegment StartX=9.005 StartY=38.09 StartZ=0 EndX=14.255 EndY=38.09 EndZ=0
    g6: LineSegment StartX=14.255 StartY=38.09 StartZ=0 EndX=14.255 EndY=42.49 EndZ=0
    g7: LineSegment StartX=14.255 StartY=42.49 StartZ=0 EndX=9.005 EndY=42.49 EndZ=0
    g8: LineSegment StartX=6.27 StartY=52.16 StartZ=0 EndX=6.27 EndY=36.09 EndZ=0
    g9: LineSegment StartX=28.27 StartY=42.16 StartZ=0 EndX=28.27 EndY=52.16 EndZ=0
    g10: LineSegment StartX=28.27 StartY=52.16 StartZ=0 EndX=6.27 EndY=52.16 EndZ=0
    g11: LineSegment StartX=6.27 StartY=36.09 StartZ=0 EndX=16.255 EndY=36.09 EndZ=0
    g12: LineSegment StartX=16.255 StartY=36.09 StartZ=0 EndX=16.255 EndY=42.16 EndZ=0
    g13: LineSegment StartX=16.255 StartY=42.16 StartZ=0 EndX=28.27 EndY=42.16 EndZ=0
    g14: GeomPoint [constr] X=17.27 Y=47.16 Z=0
    g15: GeomPoint [constr] X=11.63 Y=40.29 Z=0
    g16: GeomPoint [constr] X=17.27 Y=48.43 Z=0
    g17: GeomPoint [constr] X=17.27 Y=45.89 Z=0
  constraints (47):
    c: Coincident(g0,g1)
    c: Coincident(g1,g2)
    c: Coincident(g2,g3)
    c: Coincident(g3,g0)
    c: Vertical(g0)
    c: Vertical(g2)
    c: Horizontal(g1)
    c: Horizontal(g3)
    c: Coincident(g4,g5)
    c: Coincident(g5,g6)
    c: Coincident(g6,g7)
    c: Coincident(g7,g4)
    c: Vertical(g4)
    c: Vertical(g6)
    c: Horizontal(g5)
    c: Horizontal(g7)
    c: Coincident(g9,g10)
    c: Coincident(g10,g8)
    c: Vertical(g8)
    c: Vertical(g9)
    c: Horizontal(g10)
    c: Coincident(g11,g8)
    c: Horizontal(g11)
    c: Coincident(g12,g11)
    c: Vertical(g12)
    c: Coincident(g13,g12)
    c: Coincident(g13,g9)
    c: Horizontal(g13)
    c: Symmetric(g0,g2,g14)
    c: DistanceY(g17,g16) = 2.54
    c: Symmetric(g17,g16,g14)
    c: DistanceX(g-1,g14) = 17.27
    c: DistanceY(g-1,g14) = 47.16
    c: Vertical(g16,g17)
    c: DistanceY(g2,g9) = 2
    c: DistanceX(g2,g9) = 2
    c: DistanceX(g3,g3) = 18
    c: DistanceY(g2,g2) = 6
    c: DistanceX(g8,g0) = 2
    c: DistanceY(g9,g1) = 2
    c: Symmetric(g4,g6,g15)
    c: DistanceX(g-1,g15) = 11.63
    c: DistanceY(g6,g6) = 4.4
    c: DistanceX(g7,g7) = 5.25
    c: DistanceX(g6,g12) = 2
    c: DistanceY(g-1,g15) = 40.29
    c: DistanceY(g11,g5) = 2
FEATURE [PartDesign::Pocket] Pocket020  label="PortAccess"
  BaseFeature = -> Pocket019
  Direction = (0,0,-1)
  Length = 5
  Length2 = 5
  Profile = -> Sketch027 [Edge2,Edge1,Edge4,Edge3,Edge6,Edge5,Edge8,Edge7]
  ReferenceAxis = -> Sketch027 [N_Axis]
  Suppressed = false
  Type = 1
FEATURE [PartDesign::Pad] Pad016  label="PortTunnel"
  BaseFeature = -> Pocket020
  Direction = (0,0,1)
  Length = 7
  Length2 = 10
  Profile = -> Sketch027
  ReferenceAxis = -> Sketch027 [N_Axis]
  Refine = true
  Reversed = true
  Suppressed = false
  Type = 0
FEATURE [PartDesign::Body] Body  label="BackBody"
  AllowCompound = false
  Group = -> [Sketch,Pad,DatumPoint,DatumPoint001,DatumLine,Draft,Thickness,Sketch001,Pad001,DatumPlane,DatumPlane001,Sketch002,Pocket,Sketch003,Pad002,Pocket001,Sketch005,Pocket002,Sketch006,Pad005,Pocket003,Pocket004,Sketch007,Pad006,Fillet,Fillet001,Fillet002,Sketch008,Pad007,Sketch009,Pad008,ShapeString,Pocket011,Sketch024,Pocket017,Sketch025,Pocket018,Sketch026,Pocket019,Sketch027,Pocket020,Pad016,+1 more]
  Origin = -> Origin008
  Tip = -> Fillet004
COMPONENT P2 — recipe-attached ("Reset button", modeled in this document).
Construction recipe (the document's own serialized feature program — sketch geometry with constraints, then the solid features built on it; lengths are millimeters unless a unit is written):

FEATURE [PartDesign::SubShapeBinder] Binder001
  BindCopyOnChange = 0
  BindMode = 0
  ClaimChildren = false
  Context = -> Body001 [Binder001.]
  Fuse = false
  MakeFace = true
  OffsetFill = false
  OffsetIntersection = false
  OffsetJoinType = 0
  OffsetOpenResult = false
  PartialLoad = false
  Relative = true
  Support = -> [Body[Pocket001.]]
  _Version = 2
FEATURE [Sketcher::SketchObject] Sketch004
  ArcFitTolerance = 1e-06
  AttachmentSupport = -> [Binder001]
  ExternalGeometry = -> [Binder001]
  FullyConstrained = false
  MakeInternals = false
  MapMode = 5
  Placement = pos=(0,0,3.25) rot=(1,0,0;3.14159rad)
  sketch-geometry (3):
    g0: Circle CenterX=4.49 CenterY=-67.1 CenterZ=0 NormalX=0 NormalY=0 NormalZ=1 AngleXU=0 Radius=2.5
    g1: Circle [constr] CenterX=4.49 CenterY=-67.1 CenterZ=0 NormalX=0 NormalY=0 NormalZ=1 AngleXU=0 Radius=2.9174
    g2: Circle CenterX=4.49 CenterY=-67.1 CenterZ=0 NormalX=0 NormalY=0 NormalZ=1 AngleXU=0 Radius=1.75
  constraints (4):
    c: Coincident(g1,g0)
    c: Coincident(g2,g0)
    c: Diameter(g0) = 5
    c: Diameter(g2) = 3.5
FEATURE [PartDesign::Pad] Pad003
  Direction = (0,0,-1)
  Length = 1.3
  Length2 = 10
  Profile = -> Sketch004 [Edge1]
  ReferenceAxis = -> Sketch004 [N_Axis]
  Suppressed = false
  Type = 0
FEATURE [PartDesign::Pad] Pad004
  BaseFeature = -> Pad003
  Direction = (0,0,-1)
  Length = 7.5
  Length2 = 10
  Profile = -> Sketch004 [Edge2]
  ReferenceAxis = -> Sketch004 [N_Axis]
  Reversed = true
  Suppressed = false
  Type = 0
FEATURE [PartDesign::Chamfer] Chamfer
  Angle = 45
  Base = -> Pad004 [Edge6]
  BaseFeature = -> Pad004
  ChamferType = 0
  FlipDirection = false
  Size = 0.2
  Size2 = 1
  SupportTransform = false
  Suppressed = false
  UseAllEdges = false
FEATURE [PartDesign::Body] Body001  label="Reset button"
  AllowCompound = false
  Group = -> [Binder001,Sketch004,Pad003,Pad004,Chamfer]
  Origin = -> Origin009
  Placement = pos=(0,0,-0.85) rot=(0,0,1;0rad)
  Tip = -> Chamfer
COMPONENT P3 — recipe-attached ("Boot select button", modeled in this document).
Construction recipe (the document's own serialized feature program — sketch geometry with constraints, then the solid features built on it; lengths are millimeters unless a unit is written):

FEATURE [PartDesign::FeatureBase] Clone
  BaseFeature = -> Body001
  Suppressed = false
FEATURE [PartDesign::Body] Body002  label="Boot select button"
  AllowCompound = false
  Group = -> [Clone]
  Origin = -> Origin010
  Placement = pos=(-12.88,0,-0.85) rot=(0,0,1;0rad)
  Tip = -> Clone
COMPONENT P4 — recipe-attached ("FrontBody", modeled in this document).
Construction recipe (the document's own serialized feature program — sketch geometry with constraints, then the solid features built on it; lengths are millimeters unless a unit is written):

FEATURE [PartDesign::SubShapeBinder] Binder002  label="Side profile binder"
  BindCopyOnChange = 0
  BindMode = 0
  ClaimChildren = false
  Context = -> Body003 [Binder002.]
  Fuse = false
  MakeFace = true
  OffsetFill = false
  OffsetIntersection = false
  OffsetJoinType = 0
  OffsetOpenResult = false
  PartialLoad = false
  Relative = true
  Support = -> [Body[Sketch.]]
  _Version = 2
FEATURE [Sketcher::SketchObject] Sketch010
  ArcFitTolerance = 1e-06
  AttachmentSupport = -> [Binder002]
  ExternalGeometry = -> [Binder002]
  FullyConstrained = true
  MakeInternals = false
  MapMode = 5
  Placement = pos=(0,0,0) rot=(0.57735,0.57735,0.57735;2.0944rad)
  sketch-geometry (6):
    g0: LineSegment StartX=-5 StartY=0 StartZ=0 EndX=72 EndY=9e-16 EndZ=0
    g1: LineSegment StartX=72 StartY=9e-16 StartZ=0 EndX=71.74 EndY=-6.61778 EndZ=0
    g2: ArcOfCircle CenterX=68.7423 CenterY=-6.5 CenterZ=0 NormalX=0 NormalY=0 NormalZ=1 AngleXU=0 Radius=3 StartAngle=4.71239 EndAngle=6.24392
    g3: LineSegment StartX=68.7423 StartY=-9.5 StartZ=0 EndX=-1.7423 EndY=-9.5 EndZ=0
    g4: ArcOfCircle CenterX=-1.7423 CenterY=-6.5 CenterZ=0 NormalX=0 NormalY=0 NormalZ=1 AngleXU=0 Radius=3 StartAngle=3.18086 EndAngle=4.71239
    g5: LineSegment StartX=-4.73999 StartY=-6.61778 StartZ=0 EndX=-5 EndY=0 EndZ=0
  constraints (14):
    c: Coincident(g-3,g0)
    c: Coincident(g0,g-5)
    c: Coincident(g0,g1)
    c: Tangent(g1,g2) = 1.5708
    c: Tangent(g3,g4) = 1.5708
    c: Coincident(g5,g0)
    c: Angle(g5,g0) = 1.53153
    c: Angle(g0,g1) = 1.53153
    c: DistanceY(g3,g0) = 9.5
    c: Horizontal(g3)
    c: Tangent(g2,g3) = 1.5708
    c: Equal(g-6,g4)
    c: Equal(g4,g2)
    c: Tangent(g4,g5) = 1.5708
FEATURE [PartDesign::Pad] Pad009  label="General shape of the front thing"
  Direction = (1,0,0)
  Length = 63
  Length2 = 10
  Midplane = true
  Profile = -> Sketch010
  ReferenceAxis = -> Sketch010 [N_Axis]
  Suppressed = false
  Type = 0
FEATURE [PartDesign::Draft] Draft001  label="Sides draft front"
  Angle = 1
  Base = -> Pad009 [Face7,Face8]
  BaseFeature = -> Pad009
  SupportTransform = false
  Suppressed = false
FEATURE [PartDesign::Thickness] Thickness001  label="Digging the front"
  Base = -> Draft001 [Face1]
  BaseFeature = -> Draft001
  Intersection = false
  Join = 1
  Mode = 0
  Reversed = true
  SupportTransform = false
  Suppressed = false
  Value = 2.9
FEATURE [PartDesign::SubShapeBinder] Binder004  label="Back PCB opening binder"
  BindCopyOnChange = 0
  BindMode = 0
  ClaimChildren = false
  Context = -> Body003 [Binder004.]
  Fuse = false
  MakeFace = true
  OffsetFill = false
  OffsetIntersection = false
  OffsetJoinType = 0
  OffsetOpenResult = false
  PartialLoad = false
  Relative = true
  Support = -> [Body[Sketch005.]]
  _Version = 2
FEATURE [PartDesign::SubShapeBinder] Binder005  label="Screw column binder"
  BindCopyOnChange = 0
  BindMode = 0
  ClaimChildren = false
  Context = -> Body003 [Binder005.]
  Fuse = false
  MakeFace = true
  OffsetFill = false
  OffsetIntersection = false
  OffsetJoinType = 0
  OffsetOpenResult = false
  PartialLoad = false
  Relative = true
  Support = -> [Body[Sketch006.]]
  _Version = 2
FEATURE [PartDesign::SubShapeBinder] Binder008  label="Bottom of PCB binder"
  BindCopyOnChange = 0
  BindMode = 0
  ClaimChildren = false
  Context = -> Body003 [Binder008.]
  Fuse = false
  MakeFace = true
  OffsetFill = false
  OffsetIntersection = false
  OffsetJoinType = 0
  OffsetOpenResult = false
  PartialLoad = false
  Placement = pos=(0,0,-1.2) rot=(0,0,1;0rad)
  Relative = true
  Support = -> [Body[DatumPlane001.]]
  _Version = 2
FEATURE [PartDesign::SubShapeBinder] Binder  label="BackBinder"
  BindCopyOnChange = 0
  BindMode = 0
  ClaimChildren = false
  Context = -> Body003 [Binder.]
  Fuse = false
  MakeFace = true
  OffsetFill = false
  OffsetIntersection = false
  OffsetJoinType = 0
  OffsetOpenResult = false
  PartialLoad = false
  Relative = true
  Support = -> [Body[Fillet004.]]
  _Version = 2
FEATURE [Sketcher::SketchObject] Sketch011
  ArcFitTolerance = 1e-06
  AttachmentSupport = -> [Binder]
  FullyConstrained = true
  MakeInternals = false
  MapMode = 5
  Placement = pos=(0,0,-0.635) rot=(1,0,0;3.14159rad)
  sketch-geometry (36):
    g0: LineSegment StartX=-32.1 StartY=5.6 StartZ=0 EndX=-29.5 EndY=5.6 EndZ=0
    g1: LineSegment StartX=29.5 StartY=5.6 StartZ=0 EndX=32.1 EndY=5.6 EndZ=0
    g2: LineSegment StartX=32.1 StartY=5.6 StartZ=0 EndX=32.1 EndY=-72.6 EndZ=0
    g3: LineSegment StartX=32.1 StartY=-72.6 StartZ=0 EndX=-32.1 EndY=-72.6 EndZ=0
    g4: LineSegment StartX=-32.1 StartY=-72.6 StartZ=0 EndX=-32.1 EndY=5.6 EndZ=0
    g5: LineSegment StartX=-29.5 StartY=5.6 StartZ=0 EndX=-29.5 EndY=-12.9193 EndZ=0
    g6: LineSegment StartX=-29.5 StartY=-12.9193 StartZ=0 EndX=-20.5 EndY=-12.9193 EndZ=0
    g7: LineSegment StartX=-20.5 StartY=-12.9193 StartZ=0 EndX=-22 EndY=-14.4193 EndZ=0
    g8: LineSegment StartX=-22 StartY=-14.4193 StartZ=0 EndX=-29.5 EndY=-14.4193 EndZ=0
    g9: LineSegment StartX=-29.5 StartY=-14.4193 StartZ=0 EndX=-29.5 EndY=-22.75 EndZ=0
    g10: LineSegment StartX=-29.5 StartY=-22.75 StartZ=0 EndX=-28 EndY=-23 EndZ=0
    g11: LineSegment StartX=-28 StartY=-23 StartZ=0 EndX=-28 EndY=-24.5 EndZ=0
    g12: LineSegment StartX=-28 StartY=-24.5 StartZ=0 EndX=-29.5 EndY=-24.75 EndZ=0
    g13: LineSegment StartX=-29.5 StartY=-24.75 StartZ=0 EndX=-29.5 EndY=-64 EndZ=0
    g14: LineSegment StartX=-29.5 StartY=-64 StartZ=0 EndX=-28 EndY=-64.25 EndZ=0
    g15: LineSegment StartX=-28 StartY=-64.25 StartZ=0 EndX=-28 EndY=-65.75 EndZ=0
    g16: LineSegment StartX=-28 StartY=-65.75 StartZ=0 EndX=-29.5 EndY=-66 EndZ=0
    g17: LineSegment StartX=-29.5 StartY=-66 StartZ=0 EndX=-29.5 EndY=-69.9985 EndZ=0
    g18: LineSegment StartX=29.5 StartY=-69.9985 StartZ=0 EndX=29.5 EndY=-66 EndZ=0
    g19: LineSegment StartX=29.5 StartY=-66 StartZ=0 EndX=28 EndY=-65.75 EndZ=0
    g20: LineSegment StartX=28 StartY=-65.75 StartZ=0 EndX=28 EndY=-64.25 EndZ=0
    g21: LineSegment StartX=28 StartY=-64.25 StartZ=0 EndX=29.5 EndY=-64 EndZ=0
    g22: LineSegment StartX=29.5 StartY=-64 StartZ=0 EndX=29.5 EndY=-24.75 EndZ=0
    g23: LineSegment StartX=29.5 StartY=-24.75 StartZ=0 EndX=28 EndY=-24.5 EndZ=0
    g24: LineSegment StartX=28 StartY=-24.5 StartZ=0 EndX=28 EndY=-23 EndZ=0
    g25: LineSegment StartX=28 StartY=-23 StartZ=0 EndX=29.5 EndY=-22.75 EndZ=0
    g26: LineSegment StartX=29.5 StartY=-22.75 StartZ=0 EndX=29.5 EndY=-14.4193 EndZ=0
    g27: LineSegment StartX=29.5 StartY=-14.4193 StartZ=0 EndX=22 EndY=-14.4193 EndZ=0
    g28: LineSegment StartX=22 StartY=-14.4193 StartZ=0 EndX=20.5 EndY=-12.9193 EndZ=0
    g29: LineSegment StartX=20.5 StartY=-12.9193 StartZ=0 EndX=29.5 EndY=-12.9193 EndZ=0
    g30: LineSegment StartX=29.5 StartY=-12.9193 StartZ=0 EndX=29.5 EndY=5.6 EndZ=0
    g31: LineSegment StartX=-29.5 StartY=-69.9985 StartZ=0 EndX=-28 EndY=-69.9985 EndZ=0
    g32: LineSegment StartX=28 StartY=-69.9985 StartZ=0 EndX=29.5 EndY=-69.9985 EndZ=0
    g33: LineSegment StartX=-28 StartY=-69.9985 StartZ=0 EndX=-28 EndY=-66.75 EndZ=0
    g34: LineSegment StartX=-28 StartY=-66.75 StartZ=0 EndX=28 EndY=-66.75 EndZ=0
    g35: LineSegment StartX=28 StartY=-66.75 StartZ=0 EndX=28 EndY=-69.9985 EndZ=0
  constraints (82):
    c: Horizontal(g0)
    c: Coincident(g0,g5)
    c: Coincident(g17,g31)
    c: Coincident(g30,g1)
    c: Horizontal(g1)
    c: Coincident(g3,g4)
    c: Coincident(g1,g2)
    c: Coincident(g2,g3)
    c: Coincident(g0,g4)
    c: Coincident(g18,g32)
    c: Vertical(g4)
    c: Vertical(g2)
    c: Horizontal(g3)
    c: PointOnObject(g-13,g1)
    c: PointOnObject(g-12,g0)
    c: PointOnObject(g-11,g4)
    c: PointOnObject(g-9,g3)
    c: PointOnObject(g-14,g2)
    c: Coincident(g5,g6)
    c: Vertical(g5)
    c: Coincident(g6,g7)
    c: Coincident(g7,g8)
    c: Coincident(g8,g9)
    c: Coincident(g9,g10)
    c: Coincident(g10,g11)
    c: Coincident(g11,g12)
    c: Coincident(g12,g13)
    c: Coincident(g13,g14)
    c: Coincident(g14,g15)
    c: Coincident(g15,g16)
    c: Coincident(g16,g17)
    c: Coincident(g18,g19)
    c: Coincident(g19,g20)
    c: Coincident(g20,g21)
    c: Coincident(g21,g22)
    c: Coincident(g22,g23)
    c: Coincident(g23,g24)
    c: Coincident(g24,g25)
    c: Coincident(g25,g26)
    c: Coincident(g26,g27)
    c: Coincident(g27,g28)
    c: Coincident(g28,g29)
    c: Coincident(g29,g30)
    c: Vertical(g30)
    c: Coincident(g7,g-16)
    c: Coincident(g6,g-15)
    c: Coincident(g5,g-15)
    c: Coincident(g8,g-16)
    c: Coincident(g-19,g10)
    c: Coincident(g-19,g9)
    c: Coincident(g11,g-20)
    c: Coincident(g12,g-20)
    c: Coincident(g-17,g29)
    c: Coincident(g28,g-17)
    c: Coincident(g27,g-18)
    c: Coincident(g26,g-18)
    c: Coincident(g25,g-21)
    c: Coincident(g24,g-21)
    c: Coincident(g23,g-22)
    c: Coincident(g22,g-22)
    c: Coincident(g-23,g15)
    c: Coincident(g16,g-23)
    c: Coincident(g14,g-24)
    c: Coincident(g13,g-24)
    c: Coincident(g20,g-25)
    c: Coincident(g21,g-25)
    c: Coincident(g19,g-26)
    c: Coincident(g18,g-26)
    c: Coincident(g31,g-5)
    c: Horizontal(g31)
    c: Horizontal(g32)
    c: PointOnObject(g31,g15)
    c: PointOnObject(g32,g20)
    c: Coincident(g18,g-6)
    c: Coincident(g31,g33)
    c: Vertical(g33)
    c: Coincident(g33,g34)
    c: Horizontal(g34)
    c: Coincident(g34,g35)
    c: Coincident(g35,g32)
    c: Vertical(g35)
    c: DistanceY(g34,g19) = 1
FEATURE [PartDesign::Pocket] Pocket005  label="Remove parts that overlap the back"
  BaseFeature = -> Thickness001
  Direction = (0,0,1)
  Length = 5
  Length2 = 5
  Profile = -> Sketch011
  ReferenceAxis = -> Sketch011 [N_Axis]
  Suppressed = false
  Type = 1
FEATURE [Sketcher::SketchObject] Sketch014
  ArcFitTolerance = 1e-06
  ExternalGeometry = -> [Binder]
  FullyConstrained = true
  MakeInternals = false
  MapMode = 5
  Placement = pos=(0,12.9193,-2.9e-15) rot=(1,0,0;1.5708rad)
  sketch-geometry (4):
    g0: LineSegment StartX=-28.4844 StartY=-6.6 StartZ=0 EndX=28.4844 EndY=-6.6 EndZ=0
    g1: LineSegment StartX=28.4844 StartY=-6.6 StartZ=0 EndX=29.5 EndY=-2 EndZ=0
    g2: LineSegment StartX=29.5 StartY=-2 StartZ=0 EndX=-29.5 EndY=-2 EndZ=0
    g3: LineSegment StartX=-29.5 StartY=-2 StartZ=0 EndX=-28.4844 EndY=-6.6 EndZ=0
  constraints (8):
    c: Coincident(g-3,g0)
    c: Coincident(g0,g1)
    c: Coincident(g3,g0)
    c: Coincident(g2,g3)
    c: Coincident(g1,g2)
    c: Symmetric(g3,g1,g-2)
    c: Coincident(g0,g-3)
    c: Coincident(g2,g-5)
FEATURE [Sketcher::SketchObject] Sketch023
  ArcFitTolerance = 1e-06
  AttachmentSupport = -> [Pocket005]
  ExternalGeometry = -> [Pocket005]
  FullyConstrained = true
  MakeInternals = false
  MapMode = 5
  Placement = pos=(0,0,-0.635) rot=(0,0,1;0rad)
  sketch-geometry (8):
    g0: LineSegment StartX=30.0862 StartY=70.1451 StartZ=0 EndX=-26.7611 EndY=70.1451 EndZ=0
    g1: LineSegment StartX=-28.0111 StartY=68.8951 StartZ=0 EndX=28.4844 EndY=68.8951 EndZ=0
    g2: LineSegment StartX=28.4844 StartY=68.8951 StartZ=0 EndX=28.4844 EndY=33.8451 EndZ=0
    g3: LineSegment StartX=28.4844 StartY=33.8451 StartZ=0 EndX=30.0917 EndY=33.8451 EndZ=0
    g4: LineSegment StartX=31.4889 StartY=68.7423 StartZ=0 EndX=31.4889 EndY=35.2423 EndZ=0
    g5: LineSegment StartX=30.0917 StartY=33.8451 StartZ=0 EndX=31.4889 EndY=35.2423 EndZ=0
    g6: LineSegment StartX=30.0862 StartY=70.1451 StartZ=0 EndX=31.4889 EndY=68.7423 EndZ=0
    g7: LineSegment StartX=-28.0111 StartY=68.8951 StartZ=0 EndX=-26.7611 EndY=70.1451 EndZ=0
  constraints (24):
    c: DistanceY(g0,g-6) = 1.83
    c: DistanceX(g1,g4) = 59.5
    c: Horizontal(g1)
    c: Coincident(g2,g1)
    c: Vertical(g2)
    c: Coincident(g3,g2)
    c: Horizontal(g3)
    c: PointOnObject(g1,g-7)
    c: Horizontal(g0)
    c: Vertical(g4)
    c: PointOnObject(g4,g-6)
    c: Coincident(g5,g3)
    c: Coincident(g5,g4)
    c: Coincident(g6,g0)
    c: Coincident(g6,g4)
    c: Angle(g5,g4) = 0.785398
    c: Angle(g4,g6) = 0.785398
    c: DistanceY(g4,g4) = 33.5
    c: DistanceY(g3,g0) = 36.3
    c: Coincident(g7,g1)
    c: Coincident(g7,g0)
    c: Angle(g0,g7) = 0.785398
    c: DistanceY(g1,g0) = 1.25
    c: Horizontal(g-7,g4)
FEATURE [PartDesign::Pocket] Pocket014  label="Remove parts that overlap the PCB"
  BaseFeature = -> Pocket005
  Direction = (0,0,-1)
  Length = 1.4
  Length2 = 2
  Offset = 0.35
  Profile = -> Sketch023
  ReferenceAxis = -> Sketch023 [N_Axis]
  Suppressed = false
  Type = 4
FEATURE [Sketcher::SketchObject] Sketch012
  ArcFitTolerance = 1e-06
  ExternalGeometry = -> [Binder004,Pocket014]
  FullyConstrained = true
  MakeInternals = false
  MapMode = 5
  Placement = pos=(0,12.9193,0) rot=(1,0,0;1.5708rad)
  sketch-geometry (12):
    g0: LineSegment StartX=-29.5 StartY=-2.3416 StartZ=0 EndX=-29.5 EndY=-7 EndZ=0
    g1: ArcOfCircle CenterX=-28.5 CenterY=-7 CenterZ=0 NormalX=0 NormalY=0 NormalZ=1 AngleXU=0 Radius=1 StartAngle=3.14159 EndAngle=4.71239
    g2: LineSegment StartX=-28.5 StartY=-8 StartZ=0 EndX=28.5 EndY=-8 EndZ=0
    g3: ArcOfCircle CenterX=28.5 CenterY=-7 CenterZ=0 NormalX=0 NormalY=0 NormalZ=1 AngleXU=0 Radius=1 StartAngle=4.71239 EndAngle=6.28319
    g4: LineSegment StartX=29.5 StartY=-7 StartZ=0 EndX=29.5 EndY=-2.3416 EndZ=0
    g5: LineSegment StartX=29.5 StartY=0 StartZ=0 EndX=-29.5 EndY=0 EndZ=0
    g6: ArcOfCircle CenterX=29.5 CenterY=-0.916438 CenterZ=0 NormalX=0 NormalY=0 NormalZ=1 AngleXU=0 Radius=0.916438 StartAngle=1.5708 EndAngle=3.14159
    g7: ArcOfCircle CenterX=29.5 CenterY=-1.41644 CenterZ=0 NormalX=0 NormalY=0 NormalZ=1 AngleXU=0 Radius=0.925166 StartAngle=3.14159 EndAngle=4.71239
    g8: LineSegment StartX=28.5836 StartY=-0.916438 StartZ=0 EndX=28.5748 EndY=-1.41644 EndZ=0
    g9: ArcOfCircle CenterX=-29.5 CenterY=-0.916438 CenterZ=0 NormalX=0 NormalY=0 NormalZ=1 AngleXU=0 Radius=0.916438 StartAngle=0 EndAngle=1.5708
    g10: ArcOfCircle CenterX=-29.5 CenterY=-1.41644 CenterZ=0 NormalX=0 NormalY=0 NormalZ=1 AngleXU=0 Radius=0.925166 StartAngle=4.71239 EndAngle=6.28319
    g11: LineSegment StartX=-28.5836 StartY=-0.916438 StartZ=0 EndX=-28.5748 EndY=-1.41644 EndZ=0
  constraints (38):
    c: Vertical(g0)
    c: Tangent(g0,g1) = -1.5708
    c: Tangent(g2,g3) = -1.5708
    c: Vertical(g4)
    c: Horizontal(g2)
    c: PointOnObject(g-4,g0)
    c: Radius(g3) = 1
    c: Equal(g3,g1)
    c: Tangent(g1,g2) = -1.5708
    c: PointOnObject(g-7,g4)
    c: Tangent(g3,g4) = -1.5708
    c: DistanceY(g2,g5) = 8
    c: PointOnObject(g5,g-1)
    c: PointOnObject(g5,g-1)
    c: PointOnObject(g5,g0)
    c: PointOnObject(g5,g4)
    c: Horizontal(g0,g4)
    c: Angle(g6) = 1.5708
    c: Coincident(g6,g5)
    c: PointOnObject(g6,g4)
    c: PointOnObject(g6,g-10)
    c: Angle(g7) = 1.5708
    c: Coincident(g7,g4)
    c: PointOnObject(g7,g4)
    c: PointOnObject(g7,g-10)
    c: DistanceY(g7,g6) = 0.5
    c: Coincident(g8,g6)
    c: Coincident(g8,g7)
    c: PointOnObject(g9,g0)
    c: Coincident(g9,g5)
    c: Horizontal(g9,g9)
    c: PointOnObject(g9,g-9)
    c: Coincident(g10,g0)
    c: PointOnObject(g10,g-9)
    c: Horizontal(g10,g10)
    c: Vertical(g10,g0)
    c: Coincident(g11,g9)
    c: Coincident(g11,g10)
FEATURE [PartDesign::Pocket] Pocket006  label="Front opening"
  BaseFeature = -> Pocket014
  Direction = (0,1,0)
  Length = 5
  Length2 = 5
  Profile = -> Sketch012
  ReferenceAxis = -> Sketch012 [N_Axis]
  Refine = true
  Reversed = true
  Suppressed = false
  Type = 1
FEATURE [Sketcher::SketchObject] Sketch013
  ArcFitTolerance = 1e-06
  AttachmentOffset = pos=(0,0,-1.5) rot=(0,0,1;0rad)
  AttachmentSupport = -> [Pocket006]
  ExternalGeometry = -> [Binder005]
  FullyConstrained = true
  MakeInternals = false
  MapMode = 5
  Placement = pos=(0,0,-8.1) rot=(0,0,1;0rad)
  sketch-geometry (4):
    g0: Circle CenterX=24.5 CenterY=27 CenterZ=0 NormalX=0 NormalY=0 NormalZ=1 AngleXU=0 Radius=1.1
    g1: Circle CenterX=24.5 CenterY=27 CenterZ=0 NormalX=0 NormalY=0 NormalZ=1 AngleXU=0 Radius=2.75
    g2: Circle CenterX=-24.25 CenterY=27 CenterZ=0 NormalX=0 NormalY=0 NormalZ=1 AngleXU=0 Radius=1.1
    g3: Circle CenterX=-24.25 CenterY=27 CenterZ=0 NormalX=0 NormalY=0 NormalZ=1 AngleXU=0 Radius=2.75
  constraints (8):
    c: Coincident(g0,g-6)
    c: Equal(g0,g-6)
    c: Coincident(g1,g0)
    c: Coincident(g2,g-5)
    c: Equal(g2,g-5)
    c: Coincident(g3,g2)
    c: Equal(g-3,g1)
    c: Equal(g-4,g3)
FEATURE [PartDesign::Pad] Pad011  label="Top PCB barrier"
  BaseFeature = -> Pocket006
  Direction = (0,-1,0)
  Length = 1.5
  Length2 = 10
  Profile = -> Sketch014
  ReferenceAxis = -> Sketch014 [N_Axis]
  Refine = true
  Reversed = true
  Suppressed = false
  Type = 0
FEATURE [PartDesign::Pad] Pad017  label="Front Screw Columns"
  BaseFeature = -> Pad011
  Direction = (0,0,1)
  Length = 10
  Length2 = 10
  Profile = -> Sketch013 [Edge4,Edge2]
  ReferenceAxis = -> Sketch013 [N_Axis]
  Suppressed = false
  Type = 3
  UpToFace = -> Pad011 [Face56]
FEATURE [PartDesign::Pocket] Pocket022  label="Front Screw Holes"
  BaseFeature = -> Pad017
  Direction = (0,0,-1)
  Length = 5
  Length2 = 5
  Profile = -> Sketch013 [Edge1,Edge3]
  ReferenceAxis = -> Sketch013 [N_Axis]
  Reversed = true
  Suppressed = false
  Type = 1
FEATURE [PartDesign::SubShapeBinder] Binder010  label="GlassBinder"
  BindCopyOnChange = 0
  BindMode = 0
  ClaimChildren = false
  Context = -> Body003 [Binder010.]
  Fuse = false
  MakeFace = true
  OffsetFill = false
  OffsetIntersection = false
  OffsetJoinType = 0
  OffsetOpenResult = false
  PartialLoad = false
  Relative = true
  Support = -> [Board_9dbe[Body004.Pad019.]]
  _Version = 2
FEATURE [Sketcher::SketchObject] Sketch015
  ArcFitTolerance = 1e-06
  AttachmentSupport = -> [Pad011]
  ExternalGeometry = -> [Binder010]
  FullyConstrained = true
  MakeInternals = false
  MapMode = 5
  Placement = pos=(0,0,-6.6) rot=(0,0,1;0rad)
  sketch-geometry (15):
    g0: LineSegment StartX=25.85 StartY=68.9 StartZ=0 EndX=25.85 EndY=41.9 EndZ=0
    g1: LineSegment StartX=25.85 StartY=41.9 StartZ=0 EndX=-25.15 EndY=41.9 EndZ=0
    g2: LineSegment [constr] StartX=-25.15 StartY=41.9 StartZ=0 EndX=-25.15 EndY=68.9 EndZ=0
    g3: LineSegment StartX=-25.15 StartY=68.9 StartZ=0 EndX=25.85 EndY=68.9 EndZ=0
    g4: LineSegment StartX=30.85 StartY=44.4 StartZ=0 EndX=30.85 EndY=66.4 EndZ=0
    g5: LineSegment StartX=30.85 StartY=66.4 StartZ=0 EndX=28.85 EndY=66.4 EndZ=0
    g6: LineSegment StartX=28.85 StartY=66.4 StartZ=0 EndX=28.85 EndY=44.4 EndZ=0
    g7: LineSegment StartX=28.85 StartY=44.4 StartZ=0 EndX=30.85 EndY=44.4 EndZ=0
    g8: GeomPoint [constr] X=0.35 Y=55.4 Z=0
    g9: GeomPoint [constr] X=25.35 Y=55.4 Z=0
    g10: LineSegment [constr] StartX=25.35 StartY=55.4 StartZ=0 EndX=0.35 EndY=55.4 EndZ=0
    g11: GeomPoint [constr] X=29.85 Y=44.4 Z=0
    g12: LineSegment StartX=-25.15 StartY=41.9 StartZ=0 EndX=-27.15 EndY=41.9 EndZ=0
    g13: LineSegment StartX=-27.15 StartY=41.9 StartZ=0 EndX=-27.15 EndY=68.9 EndZ=0
    g14: LineSegment StartX=-27.15 StartY=68.9 StartZ=0 EndX=-25.15 EndY=68.9 EndZ=0
  constraints (35):
    c: Coincident(g0,g1)
    c: Coincident(g1,g2)
    c: Coincident(g2,g3)
    c: Coincident(g3,g0)
    c: Vertical(g0)
    c: Vertical(g2)
    c: Horizontal(g1)
    c: Horizontal(g3)
    c: Coincident(g4,g5)
    c: Coincident(g5,g6)
    c: Coincident(g6,g7)
    c: Coincident(g7,g4)
    c: Vertical(g4)
    c: Horizontal(g5)
    c: Horizontal(g7)
    c: Symmetric(g-3,g-4,g8)
    c: Symmetric(g0,g1,g8)
    c: DistanceX(g-3,g0) = 0.5
    c: DistanceY(g4,g4) = 22
    c: DistanceX(g7,g7) = 2
    c: Symmetric(g-3,g-3,g9)
    c: Coincident(g10,g9)
    c: Coincident(g10,g8)
    c: Symmetric(g6,g5,g10)
    c: Symmetric(g7,g7,g11)
    c: DistanceX(g11,g-5) = 1.4
    c: Coincident(g1,g12)
    c: Horizontal(g12)
    c: Coincident(g12,g13)
    c: Vertical(g13)
    c: Coincident(g13,g14)
    c: Coincident(g14,g2)
    c: Horizontal(g14)
    c: DistanceX(g12,g12) = 2
    c: DistanceY(g-3,g0) = 0.5
FEATURE [PartDesign::Pocket] Pocket007  label="Screen glass pocket001"
  BaseFeature = -> Pocket022
  Direction = (0,0,-1)
  Length = 2
  Length2 = 5
  Profile = -> Sketch015
  ReferenceAxis = -> Sketch015 [N_Axis]
  Suppressed = false
  Type = 0
FEATURE [PartDesign::SubShapeBinder] Binder011  label="DisplayPCBBinder"
  BindCopyOnChange = 0
  BindMode = 0
  ClaimChildren = false
  Context = -> Body003 [Binder011.]
  Fuse = false
  MakeFace = true
  OffsetFill = false
  OffsetIntersection = false
  OffsetJoinType = 0
  OffsetOpenResult = false
  PartialLoad = false
  Relative = true
  Support = -> [Board_9dbe[Body004.Pad018.]]
  _Version = 2
FEATURE [Sketcher::SketchObject] Sketch031
  ArcFitTolerance = 1e-06
  AttachmentSupport = -> [Binder011]
  ExternalGeometry = -> [Binder011,Pocket007]
  FullyConstrained = true
  MakeInternals = false
  MapMode = 5
  Placement = pos=(0,0,-6.6) rot=(1,0,0;3.14159rad)
  sketch-geometry (8):
    g0: LineSegment StartX=-31.4889 StartY=-41.8247 StartZ=0 EndX=-29.9642 EndY=-40.3 EndZ=0
    g1: LineSegment StartX=-29.9642 StartY=-40.3 StartZ=0 EndX=30.1642 EndY=-40.3 EndZ=0
    g2: LineSegment StartX=30.1642 StartY=-40.3 StartZ=0 EndX=31.4889 EndY=-41.6247 EndZ=0
    g3: LineSegment StartX=31.4889 StartY=-41.6247 StartZ=0 EndX=31.4889 EndY=-69.1753 EndZ=0
    g4: LineSegment StartX=31.4889 StartY=-69.1753 StartZ=0 EndX=30.1642 EndY=-70.5 EndZ=0
    g5: LineSegment StartX=30.1642 StartY=-70.5 StartZ=0 EndX=-29.9642 EndY=-70.5 EndZ=0
    g6: LineSegment StartX=-29.9642 StartY=-70.5 StartZ=0 EndX=-31.4889 EndY=-68.9753 EndZ=0
    g7: LineSegment StartX=-31.4889 StartY=-68.9753 StartZ=0 EndX=-31.4889 EndY=-41.8247 EndZ=0
  constraints (24):
    c: Coincident(g0,g1)
    c: Horizontal(g1)
    c: Coincident(g1,g2)
    c: Coincident(g2,g3)
    c: Vertical(g3)
    c: Coincident(g3,g4)
    c: Coincident(g4,g5)
    c: Horizontal(g5)
    c: Coincident(g5,g6)
    c: Coincident(g6,g7)
    c: Coincident(g7,g0)
    c: Vertical(g7)
    c: PointOnObject(g2,g-8)
    c: PointOnObject(g0,g-7)
    c: Angle(g0,g-7) = 0.785398
    c: Angle(g-8,g2) = 0.785398
    c: Angle(g-7,g6) = 0.785398
    c: Angle(g4,g-8) = 0.785398
    c: Tangent(g6,g-6)
    c: Tangent(g-3,g0)
    c: Tangent(g-4,g2)
    c: Tangent(g4,g-5)
    c: DistanceY(g4,g-5) = 0.5
    c: DistanceY(g-4,g1) = 0.5
FEATURE [PartDesign::Pocket] Pocket023  label="Display PCB opening"
  BaseFeature = -> Pocket007
  Direction = (0,0,1)
  Length = 5
  Length2 = 5
  Profile = -> Sketch031
  ReferenceAxis = -> Sketch031 [N_Axis]
  Suppressed = false
  Type = 1
FEATURE [PartDesign::SubShapeBinder] Binder012  label="Display area binder"
  BindCopyOnChange = 0
  BindMode = 0
  ClaimChildren = false
  Context = -> Body003 [Binder012.]
  Fuse = false
  MakeFace = true
  OffsetFill = false
  OffsetIntersection = false
  OffsetJoinType = 0
  OffsetOpenResult = false
  PartialLoad = false
  Relative = true
  Support = -> [Board_9dbe[Body004.Sketch030.]]
  _Version = 2
FEATURE [PartDesign::Pocket] Pocket024  label="Display Area Window"
  BaseFeature = -> Pocket023
  Direction = (0,0,-1)
  Length = 5
  Length2 = 5
  Profile = -> Binder012
  Refine = true
  Suppressed = false
  TaperAngle = 45
  Type = 0
FEATURE [Sketcher::SketchObject] Sketch020
  ArcFitTolerance = 1e-06
  FullyConstrained = true
  MakeInternals = false
  MapMode = 5
  Placement = pos=(0,0,-9.5) rot=(1,0,0;3.14159rad)
  sketch-geometry (16):
    g0: LineSegment StartX=-27 StartY=4.34038 StartZ=0 EndX=-27 EndY=-1.15962 EndZ=0
    g1: LineSegment StartX=-26.5 StartY=-1.65962 StartZ=0 EndX=-24.9 EndY=-1.65962 EndZ=0
    g2: LineSegment StartX=-24.4 StartY=-1.15962 StartZ=0 EndX=-24.4 EndY=4.34038 EndZ=0
    g3: LineSegment StartX=-24.4 StartY=4.34038 StartZ=0 EndX=-27 EndY=4.34038 EndZ=0
    g4: LineSegment StartX=24.4 StartY=4.34038 StartZ=0 EndX=24.4 EndY=-1.15962 EndZ=0
    g5: LineSegment StartX=24.9 StartY=-1.65962 StartZ=0 EndX=26.5 EndY=-1.65962 EndZ=0
    g6: LineSegment StartX=27 StartY=-1.15962 StartZ=0 EndX=27 EndY=4.34038 EndZ=0
    g7: LineSegment StartX=27 StartY=4.34038 StartZ=0 EndX=24.4 EndY=4.34038 EndZ=0
    g8: ArcOfCircle CenterX=-26.5 CenterY=-1.15962 CenterZ=0 NormalX=0 NormalY=0 NormalZ=1 AngleXU=0 Radius=0.5 StartAngle=3.14159 EndAngle=4.71239
    g9: GeomPoint [constr] X=-27 Y=-1.65962 Z=0
    g10: ArcOfCircle CenterX=-24.9 CenterY=-1.15962 CenterZ=0 NormalX=0 NormalY=0 NormalZ=1 AngleXU=0 Radius=0.5 StartAngle=4.71239 EndAngle=6.28319
    g11: GeomPoint [constr] X=-24.4 Y=-1.65962 Z=0
    g12: ArcOfCircle CenterX=24.9 CenterY=-1.15962 CenterZ=0 NormalX=0 NormalY=0 NormalZ=1 AngleXU=0 Radius=0.5 StartAngle=3.14159 EndAngle=4.71239
    g13: GeomPoint [constr] X=24.4 Y=-1.65962 Z=0
    g14: ArcOfCircle CenterX=26.5 CenterY=-1.15962 CenterZ=0 NormalX=0 NormalY=0 NormalZ=1 AngleXU=0 Radius=0.5 StartAngle=4.71239 EndAngle=6.28319
    g15: GeomPoint [constr] X=27 Y=-1.65962 Z=0
  constraints (39):
    c: Coincident(g2,g3)
    c: Coincident(g3,g0)
    c: Vertical(g0)
    c: Vertical(g2)
    c: Horizontal(g1)
    c: Horizontal(g3)
    c: Distance(g0,g2) = 2.6
    c: Distance(g9,g3) = 6
    c: Coincident(g6,g7)
    c: Coincident(g7,g4)
    c: Vertical(g4)
    c: Vertical(g6)
    c: Horizontal(g5)
    c: Horizontal(g7)
    c: DistanceX(g0,g6) = 54
    c: Symmetric(g2,g4,g-2)
    c: PointOnObject(g9,g0)
    c: PointOnObject(g9,g1)
    c: Tangent(g0,g8) = -1.5708
    c: Tangent(g1,g8) = -1.5708
    c: PointOnObject(g11,g1)
    c: PointOnObject(g11,g2)
    c: Tangent(g1,g10) = -1.5708
    c: Tangent(g2,g10) = -1.5708
    c: PointOnObject(g13,g4)
    c: PointOnObject(g13,g5)
    c: Tangent(g4,g12) = -1.5708
    c: Tangent(g5,g12) = -1.5708
    c: PointOnObject(g15,g5)
    c: PointOnObject(g15,g6)
    c: Tangent(g5,g14) = -1.5708
    c: Tangent(g6,g14) = -1.5708
    c: Radius(g8) = 0.5
    c: Equal(g8,g10)
    c: Equal(g8,g12)
    c: Equal(g8,g14)
    c: Horizontal(g5,g1)
    c: Equal(g7,g3)
    c: PointOnObject(g0,g-3)
FEATURE [PartDesign::Pocket] Pocket012  label="Slots"
  BaseFeature = -> Pocket024
  Direction = (0,1e-16,1)
  Length = 5
  Length2 = 5
  Profile = -> Sketch020
  ReferenceAxis = -> Sketch020 [N_Axis]
  Suppressed = false
  Type = 1
FEATURE [PartDesign::Fillet] Fillet005
  Base = -> Pocket012 [Edge39,Edge91]
  BaseFeature = -> Pocket012
  Radius = 1
  Refine = true
  SupportTransform = false
  Suppressed = false
  UseAllEdges = false
FEATURE [Sketcher::SketchObject] Sketch032
  ArcFitTolerance = 1e-06
  AttachmentSupport = -> [Fillet005]
  ExternalGeometry = -> [Fillet005]
  FullyConstrained = true
  MakeInternals = false
  MapMode = 5
  Placement = pos=(0,0,-0.635) rot=(0,0,1;0rad)
  sketch-geometry (8):
    g0: LineSegment StartX=-30.5 StartY=71 StartZ=0 EndX=-30.5 EndY=39.8 EndZ=0
    g1: LineSegment StartX=-30.5 StartY=39.8 StartZ=0 EndX=-29.5 EndY=39.8 EndZ=0
    g2: LineSegment StartX=-29.5 StartY=39.8 StartZ=0 EndX=-29.5 EndY=71 EndZ=0
    g3: LineSegment StartX=-29.5 StartY=71 StartZ=0 EndX=-30.5 EndY=71 EndZ=0
    g4: LineSegment StartX=29.5 StartY=71 StartZ=0 EndX=29.5 EndY=39.8 EndZ=0
    g5: LineSegment StartX=29.5 StartY=39.8 StartZ=0 EndX=30.5 EndY=39.8 EndZ=0
    g6: LineSegment StartX=30.5 StartY=39.8 StartZ=0 EndX=30.5 EndY=71 EndZ=0
    g7: LineSegment StartX=30.5 StartY=71 StartZ=0 EndX=29.5 EndY=71 EndZ=0
  constraints (24):
    c: Coincident(g0,g1)
    c: Coincident(g1,g2)
    c: Coincident(g2,g3)
    c: Coincident(g3,g0)
    c: Vertical(g0)
    c: Vertical(g2)
    c: Horizontal(g1)
    c: Horizontal(g3)
    c: Coincident(g4,g5)
    c: Coincident(g5,g6)
    c: Coincident(g6,g7)
    c: Coincident(g7,g4)
    c: Vertical(g4)
    c: Vertical(g6)
    c: Horizontal(g5)
    c: Horizontal(g7)
    c: DistanceY(g-3,g2) = 0.5
    c: Horizontal(g2,g4)
    c: DistanceY(g0,g-4) = 0.5
    c: Vertical(g-4,g1)
    c: DistanceX(g1,g1) = 1
    c: DistanceX(g5,g5) = 1
    c: DistanceY(g5,g-5) = 0.5
    c: Vertical(g4,g-6)
FEATURE [PartDesign::Pocket] Pocket025  label="PCB side pockets"
  BaseFeature = -> Fillet005
  Direction = (0,0,-1)
  Length = 0
  Length2 = 5
  Profile = -> Sketch032
  ReferenceAxis = -> Sketch032 [N_Axis]
  Refine = true
  Suppressed = false
  Type = 3
  UpToFace = -> Fillet005 [Face6]
FEATURE [PartDesign::Body] Body003  label="FrontBody"
  AllowCompound = false
  Group = -> [Binder012,Binder011,Binder010,Binder,Binder002,Sketch010,Pad009,Draft001,Thickness001,Sketch011,Pocket005,Binder004,Sketch012,Sketch023,Binder008,Pocket014,Pocket006,Pad011,Sketch013,Binder005,Pad017,Pocket022,Sketch014,Sketch015,Pocket007,Pocket023,Pocket024,Sketch031,Sketch020,Pocket012,Fillet005,Sketch032,Pocket025]
  Origin = -> Origin011
  Tip = -> Pocket025
COMPONENT P5 — recipe-attached ("Left cover", modeled in this document).
Construction recipe (the document's own serialized feature program — sketch geometry with constraints, then the solid features built on it; lengths are millimeters unless a unit is written):

FEATURE [PartDesign::SubShapeBinder] Binder013  label="Display PCB binder"
  BindCopyOnChange = 0
  BindMode = 0
  ClaimChildren = false
  Context = -> Board_9dbe [Body005.Binder013.]
  Fuse = false
  MakeFace = true
  OffsetFill = false
  OffsetIntersection = false
  OffsetJoinType = 0
  OffsetOpenResult = false
  PartialLoad = false
  Placement = pos=(0,0,-0.5) rot=(0,0,1;0rad)
  Relative = true
  Support = -> [Body004[Pad018.]]
  _Version = 2
FEATURE [PartDesign::SubShapeBinder] Binder014  label="Front body binder"
  BindCopyOnChange = 0
  BindMode = 0
  ClaimChildren = false
  Context = -> Body005 [Binder014.]
  Fuse = false
  MakeFace = true
  OffsetFill = false
  OffsetIntersection = false
  OffsetJoinType = 0
  OffsetOpenResult = false
  PartialLoad = false
  Relative = true
  Support = -> [Body003]
  _Version = 2
FEATURE [Sketcher::SketchObject] Sketch033
  ArcFitTolerance = 1e-06
  AttachmentSupport = -> [Binder013]
  ExternalGeometry = -> [Binder014,Binder013]
  FullyConstrained = true
  MakeInternals = false
  MapMode = 5
  Placement = pos=(0,0,-5.45) rot=(0,0,1;0rad)
  sketch-geometry (14):
    g0: LineSegment StartX=29.5 StartY=71 StartZ=0 EndX=30.5 EndY=71 EndZ=0
    g1: LineSegment StartX=30.5 StartY=71 StartZ=0 EndX=30.5 EndY=70.1642 EndZ=0
    g2: LineSegment StartX=30.5 StartY=70.1642 StartZ=0 EndX=32.05 EndY=68.6142 EndZ=0
    g3: LineSegment StartX=32.05 StartY=42.1858 StartZ=0 EndX=30.5 EndY=40.6358 EndZ=0
    g4: LineSegment StartX=30.5 StartY=40.6358 StartZ=0 EndX=30.5 EndY=39.8 EndZ=0
    g5: LineSegment StartX=30.5 StartY=39.8 StartZ=0 EndX=29.5 EndY=39.8 EndZ=0
    g6: LineSegment StartX=32.05 StartY=42.1858 StartZ=0 EndX=32.05 EndY=68.6142 EndZ=0
    g7: LineSegment StartX=29.5 StartY=71 StartZ=0 EndX=29.5 EndY=69.75 EndZ=0
    g8: LineSegment StartX=29.5 StartY=69.75 StartZ=0 EndX=31.25 EndY=68 EndZ=0
    g9: LineSegment StartX=31.25 StartY=68 StartZ=0 EndX=31.25 EndY=42.8 EndZ=0
    g10: LineSegment StartX=31.25 StartY=42.8 StartZ=0 EndX=29.5 EndY=41.05 EndZ=0
    g11: LineSegment StartX=29.5 StartY=41.05 StartZ=0 EndX=29.5 EndY=39.8 EndZ=0
    g12: LineSegment [constr] StartX=29.5 StartY=69.75 StartZ=0 EndX=30.5 EndY=70.1642 EndZ=0
    g13: LineSegment [constr] StartX=30.5 StartY=40.6358 StartZ=0 EndX=29.5 EndY=41.05 EndZ=0
  constraints (34):
    c: Coincident(g-4,g0)
    c: Coincident(g0,g-4)
    c: Coincident(g0,g1)
    c: Coincident(g1,g-3)
    c: Coincident(g1,g2)
    c: Coincident(g3,g-5)
    c: Coincident(g3,g4)
    c: Coincident(g4,g-6)
    c: Coincident(g4,g5)
    c: Coincident(g5,g-6)
    c: PointOnObject(g2,g-3)
    c: PointOnObject(g3,g-5)
    c: Coincident(g6,g3)
    c: Coincident(g6,g2)
    c: Vertical(g6)
    c: Coincident(g0,g7)
    c: Vertical(g7)
    c: Coincident(g7,g8)
    c: PointOnObject(g8,g-7)
    c: Coincident(g8,g9)
    c: PointOnObject(g9,g-7)
    c: Coincident(g9,g10)
    c: Coincident(g10,g11)
    c: Coincident(g11,g5)
    c: Vertical(g11)
    c: Parallel(g3,g10)
    c: Parallel(g8,g2)
    c: DistanceX(g-7,g2) = 0.8
    c: Coincident(g12,g7)
    c: Coincident(g12,g1)
    c: Angle(g12,g7) = 1.1781
    c: Coincident(g13,g3)
    c: Coincident(g13,g10)
    c: Angle(g13,g10) = 1.1781
FEATURE [PartDesign::Pad] Pad020
  Direction = (0,0,1)
  Length = 10
  Length2 = 10
  Placement = pos=(0,0,-0.5) rot=(0,0,1;0rad)
  Profile = -> Sketch033
  ReferenceAxis = -> Sketch033 [N_Axis]
  Suppressed = false
  Type = 3
  UpToFace = -> Binder014 [Face74]
FEATURE [Sketcher::SketchObject] Sketch035
  ArcFitTolerance = 1e-06
  AttachmentSupport = -> [Pad020]
  ExternalGeometry = -> [Pad020]
  FullyConstrained = true
  MakeInternals = false
  MapMode = 5
  Placement = pos=(0,0,-5.45) rot=(1,0,0;3.14159rad)
  sketch-geometry (4):
    g0: LineSegment StartX=32.05 StartY=-42.1858 StartZ=0 EndX=31.25 EndY=-41.3858 EndZ=0
    g1: LineSegment StartX=31.25 StartY=-41.3858 StartZ=0 EndX=31.25 EndY=-69.4142 EndZ=0
    g2: LineSegment StartX=31.25 StartY=-69.4142 StartZ=0 EndX=32.05 EndY=-68.6142 EndZ=0
    g3: LineSegment StartX=32.05 StartY=-68.6142 StartZ=0 EndX=32.05 EndY=-42.1858 EndZ=0
  constraints (10):
    c: Coincident(g-4,g0)
    c: PointOnObject(g0,g-4)
    c: Coincident(g0,g1)
    c: PointOnObject(g1,g-3)
    c: Vertical(g1)
    c: Coincident(g1,g2)
    c: Coincident(g2,g-3)
    c: Coincident(g2,g3)
    c: Coincident(g3,g0)
    c: PointOnObject(g0,g-5)
FEATURE [PartDesign::Pad] Pad022
  BaseFeature = -> Pad020
  Direction = (0,0,-1)
  Length = 1
  Length2 = 10
  Placement = pos=(0,0,-0.5) rot=(0,0,1;0rad)
  Profile = -> Sketch035
  ReferenceAxis = -> Sketch035 [N_Axis]
  Refine = true
  Suppressed = false
  Type = 0
FEATURE [PartDesign::Body] Body005  label="Left cover"
  AllowCompound = false
  Group = -> [Binder014,Binder013,Sketch033,Pad020,Sketch035,Pad022]
  Origin = -> Origin039
  Tip = -> Pad022
COMPONENT P6 — recipe-attached ("Right cover", modeled in this document).
Construction recipe (the document's own serialized feature program — sketch geometry with constraints, then the solid features built on it; lengths are millimeters unless a unit is written):

FEATURE [PartDesign::SubShapeBinder] Binder016  label="Front body binder for right cover"
  BindCopyOnChange = 0
  BindMode = 0
  ClaimChildren = false
  Context = -> Body006 [Binder016.]
  Fuse = false
  MakeFace = true
  OffsetFill = false
  OffsetIntersection = false
  OffsetJoinType = 0
  OffsetOpenResult = false
  PartialLoad = false
  Relative = true
  Support = -> [Body003]
  _Version = 2
FEATURE [PartDesign::SubShapeBinder] Binder017  label="Display PCB binder for the right cover"
  BindCopyOnChange = 0
  BindMode = 0
  ClaimChildren = false
  Context = -> Body006 [Binder017.]
  Fuse = false
  MakeFace = true
  OffsetFill = false
  OffsetIntersection = false
  OffsetJoinType = 0
  OffsetOpenResult = false
  PartialLoad = false
  Relative = true
  Support = -> [Board_9dbe[Body004.Pad018.]]
  _Version = 2
FEATURE [Sketcher::SketchObject] Sketch034
  ArcFitTolerance = 1e-06
  AttachmentSupport = -> [Binder017]
  ExternalGeometry = -> [Binder016]
  FullyConstrained = true
  MakeInternals = false
  MapMode = 5
  Placement = pos=(0,0,-5.35) rot=(0,0,1;0rad)
  sketch-geometry (8):
    g0: LineSegment StartX=-31.4889 StartY=68.9753 StartZ=0 EndX=-31.4889 EndY=41.8247 EndZ=0
    g1: LineSegment StartX=-31.4889 StartY=41.8247 StartZ=0 EndX=-30.5 EndY=40.8358 EndZ=0
    g2: LineSegment StartX=-30.5 StartY=40.8358 StartZ=0 EndX=-30.5 EndY=39.8 EndZ=0
    g3: LineSegment StartX=-30.5 StartY=39.8 StartZ=0 EndX=-29.5 EndY=39.8 EndZ=0
    g4: LineSegment StartX=-29.5 StartY=39.8 StartZ=0 EndX=-29.5 EndY=71 EndZ=0
    g5: LineSegment StartX=-29.5 StartY=71 StartZ=0 EndX=-30.5 EndY=71 EndZ=0
    g6: LineSegment StartX=-30.5 StartY=71 StartZ=0 EndX=-30.5 EndY=69.9642 EndZ=0
    g7: LineSegment StartX=-30.5 StartY=69.9642 StartZ=0 EndX=-31.4889 EndY=68.9753 EndZ=0
  constraints (16):
    c: Coincident(g-6,g0)
    c: Coincident(g0,g-5)
    c: Coincident(g0,g1)
    c: Coincident(g1,g-5)
    c: Coincident(g1,g2)
    c: Coincident(g2,g-4)
    c: Coincident(g2,g3)
    c: Coincident(g3,g-4)
    c: Coincident(g3,g4)
    c: Coincident(g4,g-3)
    c: Coincident(g4,g5)
    c: Coincident(g5,g-3)
    c: Coincident(g5,g6)
    c: Coincident(g6,g-6)
    c: Coincident(g6,g7)
    c: Coincident(g7,g0)
FEATURE [PartDesign::Pad] Pad021
  Direction = (0,0,1)
  Length = 10
  Length2 = 10
  Profile = -> Sketch034
  ReferenceAxis = -> Sketch034 [N_Axis]
  Suppressed = false
  Type = 3
  UpToFace = -> Binder016 [Face7]
FEATURE [PartDesign::Body] Body006  label="Right cover"
  AllowCompound = false
  Group = -> [Binder016,Binder017,Sketch034,Pad021]
  Origin = -> Origin040
  Tip = -> Pad021
PROVENANCE & LICENSES
A FreeCAD (.FCStd) document from a public repository crawl; recipes are the document's own serialized feature recipes (and, for linked parts, companion documents' recipes).
License: other.
